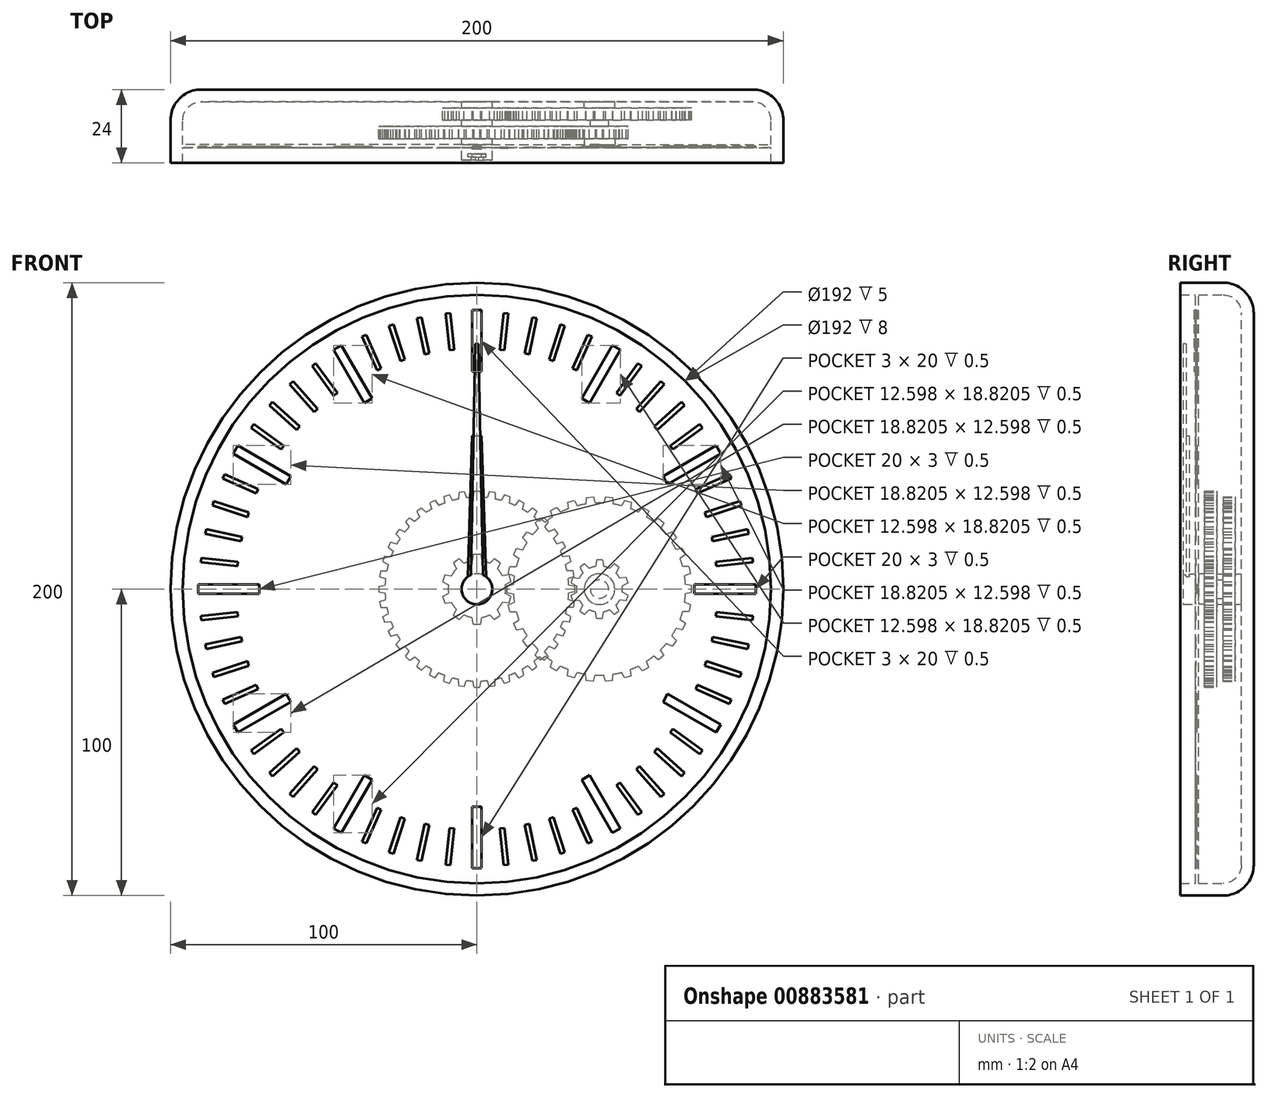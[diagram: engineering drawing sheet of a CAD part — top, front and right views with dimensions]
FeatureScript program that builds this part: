
annotation { "Feature Type Name" : "Feature", "Feature Type Description" : "" }
export const myFeature = defineFeature(function(context is Context, id is Id, definition is map)
    precondition{}
    {
        {
            var Q0;
            Q0=qCreatedBy(makeId("Front.planeOp"),FACE);
            var sketch = newSketch(context, id + "F0", { "sketchPlane" : qUnion([Q0])});
            skCircle(sketch, "E0", {"center": v(0, 0) * mm, "radius": 100 * mm});
            skSolve(sketch);
        }
        {
            var Q0;
            Q0 = qSketchRegion(id + "F0", true);
            extrude(context, id + "F1", {"entities" : qUnion([Q0]), "depth" : 24 * mm, "offsetDistance" : 25 * mm});
        }
        {
            var Q0;
            Q0=makeQuery(id+"F1.opExtrude","CAP_EDGE",EDGE,{"disambiguationData":[OSD([sQuery(id+"F0.wireOp",EDGE,"E0")])],"isStart":true});
            fillet(context, id + "F2", {"entities" : qUnion([Q0]), "radius" : 10 * mm, "tangentPropagation" : true, "allowEdgeOverflow" : false});
        }
        {
            var Q0;
            Q0=makeQuery(id+"F1.opExtrude","CAP_FACE",FACE,{"disambiguationData":[OSD([sQuery(id+"F0.wireOp",EDGE,"E0")])],"isStart":false});
            shell(context, id + "F3", {"entities" : qUnion([Q0]), "thickness" : 4 * mm});
        }
        {
            var Q0;
            {var subQ0=sQuery(id+"F0.wireOp",EDGE,"E0");Q0=makeQuery(id+"F3.opShell","OFFSET_FACE",FACE,{"disambiguationData":[OSD([subQ0]),TDD([makeQuery(id+"F1.opExtrude","CAP_FACE",FACE,{"disambiguationData":[OSD([subQ0])],"isStart":true})])]});}
            var sketch = newSketch(context, id + "F4", { "sketchPlane" : qUnion([Q0])});
            skCircle(sketch, "E1", {"center": v(0, 0) * mm, "radius": 3 * mm});
            skCircle(sketch, "E2", {"center": v(0, 0) * mm, "radius": 5 * mm});
            skCircle(sketch, "E3", {"center": v(40, 0) * mm, "radius": 3 * mm});
            skCircle(sketch, "E4", {"center": v(40, 0) * mm, "radius": 5 * mm});
            skSolve(sketch);
        }
        {
            var Q0;
            Q0 = qSketchRegion(id + "F4", true);
            extrude(context, id + "F5", {"entities" : qUnion([Q0]), "operationType" : NewBodyOperationType.ADD, "depth" : 2 * mm, "offsetDistance" : 25 * mm});
        }
        {
            var Q0;
            {var subQ0=sQuery(id+"F0.wireOp",EDGE,"E0");Q0=makeQuery(id+"F5.boolean.opBoolean","SPLIT",FACE,{"disambiguationData":[TD([makeQuery(id+"F5.opExtrude","SWEPT_FACE",FACE,{"disambiguationData":[OSD([sQuery(id+"F4.wireOp",EDGE,"E1")])]})])],"derivedFrom":makeQuery(id+"F3.opShell","OFFSET_FACE",FACE,{"disambiguationData":[OSD([subQ0]),TDD([makeQuery(id+"F1.opExtrude","CAP_FACE",FACE,{"disambiguationData":[OSD([subQ0])],"isStart":true})])]})});}
            extrude(context, id + "F6", {"entities" : qUnion([Q0]), "depth" : 19 * mm, "offsetDistance" : 25 * mm});
        }
        {
            var Q0;
            {var subQ0=sQuery(id+"F0.wireOp",EDGE,"E0");Q0=makeQuery(id+"F5.boolean.opBoolean","SPLIT",FACE,{"disambiguationData":[TD([makeQuery(id+"F5.opExtrude","SWEPT_FACE",FACE,{"disambiguationData":[OSD([sQuery(id+"F4.wireOp",EDGE,"E3")])]})])],"derivedFrom":makeQuery(id+"F3.opShell","OFFSET_FACE",FACE,{"disambiguationData":[OSD([subQ0]),TDD([makeQuery(id+"F1.opExtrude","CAP_FACE",FACE,{"disambiguationData":[OSD([subQ0])],"isStart":true})])]})});}
            extrude(context, id + "F7", {"entities" : qUnion([Q0]), "depth" : 8 * mm, "offsetDistance" : 25 * mm});
        }
        {
            var Q0;
            Q0=makeQuery(id+"F5.opExtrude","CAP_FACE",FACE,{"disambiguationData":[OSD([sQuery(id+"F4.wireOp",EDGE,"E1"),sQuery(id+"F4.wireOp",EDGE,"E2")])],"isStart":false});
            var sketch = newSketch(context, id + "F8", { "sketchPlane" : qUnion([Q0])});
            skCircle(sketch, "E5", {"center": v(0, 0) * mm, "radius": 9.38 * mm});
            skLineSegment(sketch, "E6", {"start": v(0, 11.38) * mm, "end": v(1.18, 11.38) * mm});
            skLineSegment(sketch, "E7", {"start": v(1.18, 11.38) * mm, "end": v(1.55, 9.25) * mm});
            skLineSegment(sketch, "E8.MirrorCS", {"start": v(0, 11.38) * mm, "end": v(-1.18, 11.38) * mm});
            skLineSegment(sketch, "E9.MirrorCS", {"start": v(-1.18, 11.38) * mm, "end": v(-1.55, 9.25) * mm});
            skLineSegment(sketch, "E10.1.0", {"start": v(-7.64, 8.51) * mm, "end": v(-6.7, 6.57) * mm});
            skLineSegment(sketch, "E10.1.1", {"start": v(-6.69, 9.2) * mm, "end": v(-7.64, 8.51) * mm});
            skLineSegment(sketch, "E10.1.2", {"start": v(-6.69, 9.2) * mm, "end": v(-5.73, 9.9) * mm});
            skLineSegment(sketch, "E10.1.3", {"start": v(-5.73, 9.9) * mm, "end": v(-4.18, 8.4) * mm});
            skLineSegment(sketch, "E10.2.0", {"start": v(-11.18, 2.4) * mm, "end": v(-9.27, 1.38) * mm});
            skLineSegment(sketch, "E10.2.1", {"start": v(-10.82, 3.52) * mm, "end": v(-11.18, 2.4) * mm});
            skLineSegment(sketch, "E10.2.2", {"start": v(-10.82, 3.52) * mm, "end": v(-10.45, 4.64) * mm});
            skLineSegment(sketch, "E10.2.3", {"start": v(-10.45, 4.64) * mm, "end": v(-8.31, 4.33) * mm});
            skLineSegment(sketch, "E11.2.3.0", {"start": v(-10.45, -4.64) * mm, "end": v(-8.31, -4.33) * mm});
            skLineSegment(sketch, "E11.3.3.0", {"start": v(-10.82, -3.52) * mm, "end": v(-10.45, -4.64) * mm});
            skLineSegment(sketch, "E11.6.3.0", {"start": v(-10.82, -3.52) * mm, "end": v(-11.18, -2.4) * mm});
            skLineSegment(sketch, "E11.9.3.0", {"start": v(-11.18, -2.4) * mm, "end": v(-9.27, -1.38) * mm});
            skLineSegment(sketch, "E11.2.4.0", {"start": v(-5.73, -9.9) * mm, "end": v(-4.18, -8.4) * mm});
            skLineSegment(sketch, "E11.3.4.0", {"start": v(-6.69, -9.2) * mm, "end": v(-5.73, -9.9) * mm});
            skLineSegment(sketch, "E11.6.4.0", {"start": v(-6.69, -9.2) * mm, "end": v(-7.64, -8.51) * mm});
            skLineSegment(sketch, "E11.9.4.0", {"start": v(-7.64, -8.51) * mm, "end": v(-6.7, -6.57) * mm});
            skLineSegment(sketch, "E11.2.5.0", {"start": v(1.18, -11.38) * mm, "end": v(1.55, -9.25) * mm});
            skLineSegment(sketch, "E11.3.5.0", {"start": v(0, -11.38) * mm, "end": v(1.18, -11.38) * mm});
            skLineSegment(sketch, "E11.6.5.0", {"start": v(0, -11.38) * mm, "end": v(-1.18, -11.38) * mm});
            skLineSegment(sketch, "E11.9.5.0", {"start": v(-1.18, -11.38) * mm, "end": v(-1.55, -9.25) * mm});
            skLineSegment(sketch, "E11.2.6.0", {"start": v(7.64, -8.51) * mm, "end": v(6.7, -6.57) * mm});
            skLineSegment(sketch, "E11.3.6.0", {"start": v(6.69, -9.2) * mm, "end": v(7.64, -8.51) * mm});
            skLineSegment(sketch, "E11.6.6.0", {"start": v(6.69, -9.2) * mm, "end": v(5.73, -9.9) * mm});
            skLineSegment(sketch, "E11.9.6.0", {"start": v(5.73, -9.9) * mm, "end": v(4.18, -8.4) * mm});
            skLineSegment(sketch, "E11.2.7.0", {"start": v(11.18, -2.4) * mm, "end": v(9.27, -1.38) * mm});
            skLineSegment(sketch, "E11.3.7.0", {"start": v(10.82, -3.52) * mm, "end": v(11.18, -2.4) * mm});
            skLineSegment(sketch, "E11.6.7.0", {"start": v(10.82, -3.52) * mm, "end": v(10.45, -4.64) * mm});
            skLineSegment(sketch, "E11.9.7.0", {"start": v(10.45, -4.64) * mm, "end": v(8.31, -4.33) * mm});
            skLineSegment(sketch, "E11.2.8.0", {"start": v(10.45, 4.64) * mm, "end": v(8.31, 4.33) * mm});
            skLineSegment(sketch, "E11.3.8.0", {"start": v(10.82, 3.52) * mm, "end": v(10.45, 4.64) * mm});
            skLineSegment(sketch, "E11.6.8.0", {"start": v(10.82, 3.52) * mm, "end": v(11.18, 2.4) * mm});
            skLineSegment(sketch, "E11.9.8.0", {"start": v(11.18, 2.4) * mm, "end": v(9.27, 1.38) * mm});
            skLineSegment(sketch, "E11.2.9.0", {"start": v(5.73, 9.9) * mm, "end": v(4.18, 8.4) * mm});
            skLineSegment(sketch, "E11.3.9.0", {"start": v(6.69, 9.2) * mm, "end": v(5.73, 9.9) * mm});
            skLineSegment(sketch, "E11.6.9.0", {"start": v(6.69, 9.2) * mm, "end": v(7.64, 8.51) * mm});
            skLineSegment(sketch, "E11.9.9.0", {"start": v(7.64, 8.51) * mm, "end": v(6.7, 6.57) * mm});
            skSolve(sketch);
        }
        {
            var Q0;
            Q0 = qSketchRegion(id + "F8", true);
            extrude(context, id + "F9", {"entities" : qUnion([Q0]), "operationType" : NewBodyOperationType.ADD, "depth" : 4 * mm, "offsetDistance" : 25 * mm});
        }
        {
            var Q0;
            Q0=makeQuery(id+"F5.opExtrude","CAP_FACE",FACE,{"disambiguationData":[OSD([sQuery(id+"F4.wireOp",EDGE,"E3"),sQuery(id+"F4.wireOp",EDGE,"E4")])],"isStart":false});
            var sketch = newSketch(context, id + "F10", { "sketchPlane" : qUnion([Q0])});
            skCircle(sketch, "E12", {"center": v(40, 0) * mm, "radius": 28.12 * mm});
            skLineSegment(sketch, "E13", {"start": v(9.88, 0) * mm, "end": v(9.88, 1.18) * mm});
            skLineSegment(sketch, "E14", {"start": v(9.88, 1.18) * mm, "end": v(11.92, 1.54) * mm});
            skLineSegment(sketch, "E15.MirrorCS", {"start": v(9.88, 0) * mm, "end": v(9.88, -1.18) * mm});
            skLineSegment(sketch, "E16.MirrorCS", {"start": v(9.88, -1.18) * mm, "end": v(11.92, -1.54) * mm});
            skLineSegment(sketch, "E17.1.0", {"start": v(10.29, -5.11) * mm, "end": v(12.21, -4.33) * mm});
            skLineSegment(sketch, "E17.1.1", {"start": v(10.53, -6.26) * mm, "end": v(10.29, -5.11) * mm});
            skLineSegment(sketch, "E17.1.2", {"start": v(10.53, -6.26) * mm, "end": v(10.78, -7.42) * mm});
            skLineSegment(sketch, "E17.1.3", {"start": v(10.78, -7.42) * mm, "end": v(12.85, -7.34) * mm});
            skLineSegment(sketch, "E17.2.0", {"start": v(12, -11.18) * mm, "end": v(13.72, -10.02) * mm});
            skLineSegment(sketch, "E17.2.1", {"start": v(12.48, -12.25) * mm, "end": v(12, -11.18) * mm});
            skLineSegment(sketch, "E17.2.2", {"start": v(12.48, -12.25) * mm, "end": v(12.96, -13.33) * mm});
            skLineSegment(sketch, "E17.2.3", {"start": v(12.96, -13.33) * mm, "end": v(14.97, -12.83) * mm});
            skLineSegment(sketch, "E18.1.3.0", {"start": v(14.94, -16.75) * mm, "end": v(16.38, -15.26) * mm});
            skLineSegment(sketch, "E18.3.3.0", {"start": v(15.63, -17.7) * mm, "end": v(14.94, -16.75) * mm});
            skLineSegment(sketch, "E18.6.3.0", {"start": v(15.63, -17.7) * mm, "end": v(16.32, -18.66) * mm});
            skLineSegment(sketch, "E18.9.3.0", {"start": v(16.32, -18.66) * mm, "end": v(18.18, -17.75) * mm});
            skLineSegment(sketch, "E18.1.4.0", {"start": v(18.97, -21.6) * mm, "end": v(20.07, -19.84) * mm});
            skLineSegment(sketch, "E18.3.4.0", {"start": v(19.84, -22.39) * mm, "end": v(18.97, -21.6) * mm});
            skLineSegment(sketch, "E18.6.4.0", {"start": v(19.84, -22.39) * mm, "end": v(20.72, -23.18) * mm});
            skLineSegment(sketch, "E18.9.4.0", {"start": v(20.72, -23.18) * mm, "end": v(22.35, -21.9) * mm});
            skLineSegment(sketch, "E18.1.5.0", {"start": v(23.92, -25.5) * mm, "end": v(24.63, -23.55) * mm});
            skLineSegment(sketch, "E18.3.5.0", {"start": v(24.94, -26.09) * mm, "end": v(23.92, -25.5) * mm});
            skLineSegment(sketch, "E18.6.5.0", {"start": v(24.94, -26.09) * mm, "end": v(25.96, -26.68) * mm});
            skLineSegment(sketch, "E18.9.5.0", {"start": v(25.96, -26.68) * mm, "end": v(27.3, -25.09) * mm});
            skLineSegment(sketch, "E18.1.6.0", {"start": v(29.57, -28.29) * mm, "end": v(29.86, -26.23) * mm});
            skLineSegment(sketch, "E18.3.6.0", {"start": v(30.7, -28.65) * mm, "end": v(29.57, -28.29) * mm});
            skLineSegment(sketch, "E18.6.6.0", {"start": v(30.7, -28.65) * mm, "end": v(31.81, -29.01) * mm});
            skLineSegment(sketch, "E18.9.6.0", {"start": v(31.81, -29.01) * mm, "end": v(32.78, -27.18) * mm});
            skLineSegment(sketch, "E18.1.7.0", {"start": v(35.68, -29.84) * mm, "end": v(35.53, -27.77) * mm});
            skLineSegment(sketch, "E18.3.7.0", {"start": v(36.85, -29.96) * mm, "end": v(35.68, -29.84) * mm});
            skLineSegment(sketch, "E18.6.7.0", {"start": v(36.85, -29.96) * mm, "end": v(38.02, -30.08) * mm});
            skLineSegment(sketch, "E18.9.7.0", {"start": v(38.02, -30.08) * mm, "end": v(38.6, -28.09) * mm});
            skLineSegment(sketch, "E18.1.8.0", {"start": v(41.98, -30.08) * mm, "end": v(41.4, -28.09) * mm});
            skLineSegment(sketch, "E18.3.8.0", {"start": v(43.15, -29.96) * mm, "end": v(41.98, -30.08) * mm});
            skLineSegment(sketch, "E18.6.8.0", {"start": v(43.15, -29.96) * mm, "end": v(44.32, -29.84) * mm});
            skLineSegment(sketch, "E18.9.8.0", {"start": v(44.32, -29.84) * mm, "end": v(44.47, -27.77) * mm});
            skLineSegment(sketch, "E18.1.9.0", {"start": v(48.19, -29.01) * mm, "end": v(47.22, -27.18) * mm});
            skLineSegment(sketch, "E18.3.9.0", {"start": v(49.3, -28.65) * mm, "end": v(48.19, -29.01) * mm});
            skLineSegment(sketch, "E18.6.9.0", {"start": v(49.3, -28.65) * mm, "end": v(50.43, -28.29) * mm});
            skLineSegment(sketch, "E18.9.9.0", {"start": v(50.43, -28.29) * mm, "end": v(50.14, -26.23) * mm});
            skLineSegment(sketch, "E18.1.10.0", {"start": v(54.04, -26.68) * mm, "end": v(52.7, -25.09) * mm});
            skLineSegment(sketch, "E18.3.10.0", {"start": v(55.06, -26.09) * mm, "end": v(54.04, -26.68) * mm});
            skLineSegment(sketch, "E18.6.10.0", {"start": v(55.06, -26.09) * mm, "end": v(56.08, -25.5) * mm});
            skLineSegment(sketch, "E18.9.10.0", {"start": v(56.08, -25.5) * mm, "end": v(55.37, -23.55) * mm});
            skLineSegment(sketch, "E18.1.11.0", {"start": v(59.28, -23.18) * mm, "end": v(57.65, -21.9) * mm});
            skLineSegment(sketch, "E18.3.11.0", {"start": v(60.16, -22.39) * mm, "end": v(59.28, -23.18) * mm});
            skLineSegment(sketch, "E18.6.11.0", {"start": v(60.16, -22.39) * mm, "end": v(61.03, -21.6) * mm});
            skLineSegment(sketch, "E18.9.11.0", {"start": v(61.03, -21.6) * mm, "end": v(59.93, -19.84) * mm});
            skLineSegment(sketch, "E18.1.12.0", {"start": v(63.68, -18.66) * mm, "end": v(61.82, -17.75) * mm});
            skLineSegment(sketch, "E18.3.12.0", {"start": v(64.37, -17.7) * mm, "end": v(63.68, -18.66) * mm});
            skLineSegment(sketch, "E18.6.12.0", {"start": v(64.37, -17.7) * mm, "end": v(65.06, -16.75) * mm});
            skLineSegment(sketch, "E18.9.12.0", {"start": v(65.06, -16.75) * mm, "end": v(63.62, -15.26) * mm});
            skLineSegment(sketch, "E18.1.13.0", {"start": v(67.04, -13.33) * mm, "end": v(65.03, -12.83) * mm});
            skLineSegment(sketch, "E18.3.13.0", {"start": v(67.52, -12.25) * mm, "end": v(67.04, -13.33) * mm});
            skLineSegment(sketch, "E18.6.13.0", {"start": v(67.52, -12.25) * mm, "end": v(68, -11.18) * mm});
            skLineSegment(sketch, "E18.9.13.0", {"start": v(68, -11.18) * mm, "end": v(66.28, -10.02) * mm});
            skLineSegment(sketch, "E18.1.14.0", {"start": v(69.22, -7.42) * mm, "end": v(67.15, -7.34) * mm});
            skLineSegment(sketch, "E18.3.14.0", {"start": v(69.47, -6.26) * mm, "end": v(69.22, -7.42) * mm});
            skLineSegment(sketch, "E18.6.14.0", {"start": v(69.47, -6.26) * mm, "end": v(69.71, -5.11) * mm});
            skLineSegment(sketch, "E18.9.14.0", {"start": v(69.71, -5.11) * mm, "end": v(67.79, -4.33) * mm});
            skLineSegment(sketch, "E18.1.15.0", {"start": v(70.12, -1.18) * mm, "end": v(68.08, -1.54) * mm});
            skLineSegment(sketch, "E18.3.15.0", {"start": v(70.12, 0) * mm, "end": v(70.12, -1.18) * mm});
            skLineSegment(sketch, "E18.6.15.0", {"start": v(70.12, 0) * mm, "end": v(70.12, 1.18) * mm});
            skLineSegment(sketch, "E18.9.15.0", {"start": v(70.12, 1.18) * mm, "end": v(68.08, 1.54) * mm});
            skLineSegment(sketch, "E18.1.16.0", {"start": v(69.71, 5.11) * mm, "end": v(67.79, 4.33) * mm});
            skLineSegment(sketch, "E18.3.16.0", {"start": v(69.47, 6.26) * mm, "end": v(69.71, 5.11) * mm});
            skLineSegment(sketch, "E18.6.16.0", {"start": v(69.47, 6.26) * mm, "end": v(69.22, 7.42) * mm});
            skLineSegment(sketch, "E18.9.16.0", {"start": v(69.22, 7.42) * mm, "end": v(67.15, 7.34) * mm});
            skLineSegment(sketch, "E18.1.17.0", {"start": v(68, 11.18) * mm, "end": v(66.28, 10.02) * mm});
            skLineSegment(sketch, "E18.3.17.0", {"start": v(67.52, 12.25) * mm, "end": v(68, 11.18) * mm});
            skLineSegment(sketch, "E18.6.17.0", {"start": v(67.52, 12.25) * mm, "end": v(67.04, 13.33) * mm});
            skLineSegment(sketch, "E18.9.17.0", {"start": v(67.04, 13.33) * mm, "end": v(65.03, 12.83) * mm});
            skLineSegment(sketch, "E18.1.18.0", {"start": v(65.06, 16.75) * mm, "end": v(63.62, 15.26) * mm});
            skLineSegment(sketch, "E18.3.18.0", {"start": v(64.37, 17.7) * mm, "end": v(65.06, 16.75) * mm});
            skLineSegment(sketch, "E18.6.18.0", {"start": v(64.37, 17.7) * mm, "end": v(63.68, 18.66) * mm});
            skLineSegment(sketch, "E18.9.18.0", {"start": v(63.68, 18.66) * mm, "end": v(61.82, 17.75) * mm});
            skLineSegment(sketch, "E18.1.19.0", {"start": v(61.03, 21.6) * mm, "end": v(59.93, 19.84) * mm});
            skLineSegment(sketch, "E18.3.19.0", {"start": v(60.16, 22.39) * mm, "end": v(61.03, 21.6) * mm});
            skLineSegment(sketch, "E18.6.19.0", {"start": v(60.16, 22.39) * mm, "end": v(59.28, 23.18) * mm});
            skLineSegment(sketch, "E18.9.19.0", {"start": v(59.28, 23.18) * mm, "end": v(57.65, 21.9) * mm});
            skLineSegment(sketch, "E18.1.20.0", {"start": v(56.08, 25.5) * mm, "end": v(55.37, 23.55) * mm});
            skLineSegment(sketch, "E18.3.20.0", {"start": v(55.06, 26.09) * mm, "end": v(56.08, 25.5) * mm});
            skLineSegment(sketch, "E18.6.20.0", {"start": v(55.06, 26.09) * mm, "end": v(54.04, 26.68) * mm});
            skLineSegment(sketch, "E18.9.20.0", {"start": v(54.04, 26.68) * mm, "end": v(52.7, 25.09) * mm});
            skLineSegment(sketch, "E18.1.21.0", {"start": v(50.43, 28.29) * mm, "end": v(50.14, 26.23) * mm});
            skLineSegment(sketch, "E18.3.21.0", {"start": v(49.3, 28.65) * mm, "end": v(50.43, 28.29) * mm});
            skLineSegment(sketch, "E18.6.21.0", {"start": v(49.3, 28.65) * mm, "end": v(48.19, 29.01) * mm});
            skLineSegment(sketch, "E18.9.21.0", {"start": v(48.19, 29.01) * mm, "end": v(47.22, 27.18) * mm});
            skLineSegment(sketch, "E18.1.22.0", {"start": v(44.32, 29.84) * mm, "end": v(44.47, 27.77) * mm});
            skLineSegment(sketch, "E18.3.22.0", {"start": v(43.15, 29.96) * mm, "end": v(44.32, 29.84) * mm});
            skLineSegment(sketch, "E18.6.22.0", {"start": v(43.15, 29.96) * mm, "end": v(41.98, 30.08) * mm});
            skLineSegment(sketch, "E18.9.22.0", {"start": v(41.98, 30.08) * mm, "end": v(41.4, 28.09) * mm});
            skLineSegment(sketch, "E18.1.23.0", {"start": v(38.02, 30.08) * mm, "end": v(38.6, 28.09) * mm});
            skLineSegment(sketch, "E18.3.23.0", {"start": v(36.85, 29.96) * mm, "end": v(38.02, 30.08) * mm});
            skLineSegment(sketch, "E18.6.23.0", {"start": v(36.85, 29.96) * mm, "end": v(35.68, 29.84) * mm});
            skLineSegment(sketch, "E18.9.23.0", {"start": v(35.68, 29.84) * mm, "end": v(35.53, 27.77) * mm});
            skLineSegment(sketch, "E18.1.24.0", {"start": v(31.81, 29.01) * mm, "end": v(32.78, 27.18) * mm});
            skLineSegment(sketch, "E18.3.24.0", {"start": v(30.7, 28.65) * mm, "end": v(31.81, 29.01) * mm});
            skLineSegment(sketch, "E18.6.24.0", {"start": v(30.7, 28.65) * mm, "end": v(29.57, 28.29) * mm});
            skLineSegment(sketch, "E18.9.24.0", {"start": v(29.57, 28.29) * mm, "end": v(29.86, 26.23) * mm});
            skLineSegment(sketch, "E18.1.25.0", {"start": v(25.96, 26.68) * mm, "end": v(27.3, 25.09) * mm});
            skLineSegment(sketch, "E18.3.25.0", {"start": v(24.94, 26.09) * mm, "end": v(25.96, 26.68) * mm});
            skLineSegment(sketch, "E18.6.25.0", {"start": v(24.94, 26.09) * mm, "end": v(23.92, 25.5) * mm});
            skLineSegment(sketch, "E18.9.25.0", {"start": v(23.92, 25.5) * mm, "end": v(24.63, 23.55) * mm});
            skLineSegment(sketch, "E18.1.26.0", {"start": v(20.72, 23.18) * mm, "end": v(22.35, 21.9) * mm});
            skLineSegment(sketch, "E18.3.26.0", {"start": v(19.84, 22.39) * mm, "end": v(20.72, 23.18) * mm});
            skLineSegment(sketch, "E18.6.26.0", {"start": v(19.84, 22.39) * mm, "end": v(18.97, 21.6) * mm});
            skLineSegment(sketch, "E18.9.26.0", {"start": v(18.97, 21.6) * mm, "end": v(20.07, 19.84) * mm});
            skLineSegment(sketch, "E18.1.27.0", {"start": v(16.32, 18.66) * mm, "end": v(18.18, 17.75) * mm});
            skLineSegment(sketch, "E18.3.27.0", {"start": v(15.63, 17.7) * mm, "end": v(16.32, 18.66) * mm});
            skLineSegment(sketch, "E18.6.27.0", {"start": v(15.63, 17.7) * mm, "end": v(14.94, 16.75) * mm});
            skLineSegment(sketch, "E18.9.27.0", {"start": v(14.94, 16.75) * mm, "end": v(16.38, 15.26) * mm});
            skLineSegment(sketch, "E18.1.28.0", {"start": v(12.96, 13.33) * mm, "end": v(14.97, 12.83) * mm});
            skLineSegment(sketch, "E18.3.28.0", {"start": v(12.48, 12.25) * mm, "end": v(12.96, 13.33) * mm});
            skLineSegment(sketch, "E18.6.28.0", {"start": v(12.48, 12.25) * mm, "end": v(12, 11.18) * mm});
            skLineSegment(sketch, "E18.9.28.0", {"start": v(12, 11.18) * mm, "end": v(13.72, 10.02) * mm});
            skLineSegment(sketch, "E18.1.29.0", {"start": v(10.78, 7.42) * mm, "end": v(12.85, 7.34) * mm});
            skLineSegment(sketch, "E18.3.29.0", {"start": v(10.53, 6.26) * mm, "end": v(10.78, 7.42) * mm});
            skLineSegment(sketch, "E18.6.29.0", {"start": v(10.53, 6.26) * mm, "end": v(10.29, 5.11) * mm});
            skLineSegment(sketch, "E18.9.29.0", {"start": v(10.29, 5.11) * mm, "end": v(12.21, 4.33) * mm});
            skSolve(sketch);
        }
        {
            var Q0;
            Q0 = qSketchRegion(id + "F10", true);
            extrude(context, id + "F11", {"entities" : qUnion([Q0]), "operationType" : NewBodyOperationType.ADD, "depth" : 4 * mm, "offsetDistance" : 25 * mm});
        }
        {
            var Q0;
            Q0=makeQuery(id+"F9.opExtrude","CAP_FACE",FACE,{"disambiguationData":[OSD([sQuery(id+"F8.wireOp",EDGE,"E5"),sQuery(id+"F8.wireOp",EDGE,"E6"),sQuery(id+"F8.wireOp",EDGE,"E7"),sQuery(id+"F8.wireOp",EDGE,"E8.MirrorCS"),sQuery(id+"F8.wireOp",EDGE,"E9.MirrorCS"),sQuery(id+"F8.wireOp",EDGE,"E10.1.0"),sQuery(id+"F8.wireOp",EDGE,"E10.1.1"),sQuery(id+"F8.wireOp",EDGE,"E10.1.2"),sQuery(id+"F8.wireOp",EDGE,"E10.1.3"),sQuery(id+"F8.wireOp",EDGE,"E10.2.0"),sQuery(id+"F8.wireOp",EDGE,"E10.2.1"),sQuery(id+"F8.wireOp",EDGE,"E10.2.2"),sQuery(id+"F8.wireOp",EDGE,"E10.2.3"),sQuery(id+"F8.wireOp",EDGE,"E11.2.3.0"),sQuery(id+"F8.wireOp",EDGE,"E11.3.3.0"),sQuery(id+"F8.wireOp",EDGE,"E11.6.3.0"),sQuery(id+"F8.wireOp",EDGE,"E11.9.3.0"),sQuery(id+"F8.wireOp",EDGE,"E11.2.4.0"),sQuery(id+"F8.wireOp",EDGE,"E11.3.4.0"),sQuery(id+"F8.wireOp",EDGE,"E11.6.4.0"),sQuery(id+"F8.wireOp",EDGE,"E11.9.4.0"),sQuery(id+"F8.wireOp",EDGE,"E11.2.5.0"),sQuery(id+"F8.wireOp",EDGE,"E11.3.5.0"),sQuery(id+"F8.wireOp",EDGE,"E11.6.5.0"),sQuery(id+"F8.wireOp",EDGE,"E11.9.5.0"),sQuery(id+"F8.wireOp",EDGE,"E11.2.6.0"),sQuery(id+"F8.wireOp",EDGE,"E11.3.6.0"),sQuery(id+"F8.wireOp",EDGE,"E11.6.6.0"),sQuery(id+"F8.wireOp",EDGE,"E11.9.6.0"),sQuery(id+"F8.wireOp",EDGE,"E11.2.7.0"),sQuery(id+"F8.wireOp",EDGE,"E11.3.7.0"),sQuery(id+"F8.wireOp",EDGE,"E11.6.7.0"),sQuery(id+"F8.wireOp",EDGE,"E11.9.7.0"),sQuery(id+"F8.wireOp",EDGE,"E11.2.8.0"),sQuery(id+"F8.wireOp",EDGE,"E11.3.8.0"),sQuery(id+"F8.wireOp",EDGE,"E11.6.8.0"),sQuery(id+"F8.wireOp",EDGE,"E11.9.8.0"),sQuery(id+"F8.wireOp",EDGE,"E11.2.9.0"),sQuery(id+"F8.wireOp",EDGE,"E11.3.9.0"),sQuery(id+"F8.wireOp",EDGE,"E11.6.9.0"),sQuery(id+"F8.wireOp",EDGE,"E11.9.9.0")])],"isStart":false});
            var sketch = newSketch(context, id + "F12", { "sketchPlane" : qUnion([Q0])});
            skCircle(sketch, "E19.0.0", {"center": v(0, 0) * mm, "radius": 3 * mm});
            skCircle(sketch, "E20.0", {"center": v(0, 0) * mm, "radius": 5 * mm});
            skSolve(sketch);
        }
        {
            var Q0;
            Q0 = qSketchRegion(id + "F12", true);
            extrude(context, id + "F13", {"entities" : qUnion([Q0]), "depth" : 2 * mm, "offsetDistance" : 25 * mm});
        }
        {
            var Q0;
            Q0=makeQuery(id+"F13.opExtrude","CAP_FACE",FACE,{"disambiguationData":[OSD([sQuery(id+"F12.wireOp",EDGE,"E19.0.0"),sQuery(id+"F12.wireOp",EDGE,"E20.0")])],"isStart":false});
            var sketch = newSketch(context, id + "F14", { "sketchPlane" : qUnion([Q0])});
            skCircle(sketch, "E21.0", {"center": v(0, 0) * mm, "radius": 3 * mm});
            skCircle(sketch, "E22", {"center": v(0, 0) * mm, "radius": 30 * mm});
            skLineSegment(sketch, "E23", {"start": v(0, 32) * mm, "end": v(0.94, 32) * mm});
            skLineSegment(sketch, "E24", {"start": v(0.94, 32) * mm, "end": v(1.3, 29.97) * mm});
            skLineSegment(sketch, "E25.MirrorCS", {"start": v(0, 32) * mm, "end": v(-0.94, 32) * mm});
            skLineSegment(sketch, "E26.MirrorCS", {"start": v(-0.94, 32) * mm, "end": v(-1.3, 29.97) * mm});
            skLineSegment(sketch, "E27.1.0", {"start": v(-5, 31.6) * mm, "end": v(-4.08, 31.75) * mm});
            skLineSegment(sketch, "E27.1.1", {"start": v(-5, 31.6) * mm, "end": v(-5.94, 31.46) * mm});
            skLineSegment(sketch, "E27.1.2", {"start": v(-5.94, 31.46) * mm, "end": v(-5.97, 29.4) * mm});
            skLineSegment(sketch, "E27.1.3", {"start": v(-4.08, 31.75) * mm, "end": v(-3.4, 29.8) * mm});
            skLineSegment(sketch, "E27.2.0", {"start": v(-9.89, 30.43) * mm, "end": v(-9, 30.73) * mm});
            skLineSegment(sketch, "E27.2.1", {"start": v(-9.89, 30.43) * mm, "end": v(-10.78, 30.14) * mm});
            skLineSegment(sketch, "E27.2.2", {"start": v(-10.78, 30.14) * mm, "end": v(-10.5, 28.1) * mm});
            skLineSegment(sketch, "E27.2.3", {"start": v(-9, 30.73) * mm, "end": v(-8.03, 28.9) * mm});
            skLineSegment(sketch, "E28.1.3.0", {"start": v(-14.53, 28.51) * mm, "end": v(-13.69, 28.94) * mm});
            skLineSegment(sketch, "E28.3.3.0", {"start": v(-14.53, 28.51) * mm, "end": v(-15.37, 28.08) * mm});
            skLineSegment(sketch, "E28.6.3.0", {"start": v(-15.37, 28.08) * mm, "end": v(-14.77, 26.11) * mm});
            skLineSegment(sketch, "E28.9.3.0", {"start": v(-13.69, 28.94) * mm, "end": v(-12.45, 27.3) * mm});
            skLineSegment(sketch, "E28.1.4.0", {"start": v(-18.8, 25.89) * mm, "end": v(-18.05, 26.44) * mm});
            skLineSegment(sketch, "E28.3.4.0", {"start": v(-18.8, 25.89) * mm, "end": v(-19.57, 25.33) * mm});
            skLineSegment(sketch, "E28.6.4.0", {"start": v(-19.57, 25.33) * mm, "end": v(-18.67, 23.48) * mm});
            skLineSegment(sketch, "E28.9.4.0", {"start": v(-18.05, 26.44) * mm, "end": v(-16.57, 25.01) * mm});
            skLineSegment(sketch, "E28.1.5.0", {"start": v(-22.63, 22.63) * mm, "end": v(-21.96, 23.3) * mm});
            skLineSegment(sketch, "E28.3.5.0", {"start": v(-22.63, 22.63) * mm, "end": v(-23.3, 21.96) * mm});
            skLineSegment(sketch, "E28.6.5.0", {"start": v(-23.3, 21.96) * mm, "end": v(-22.11, 20.27) * mm});
            skLineSegment(sketch, "E28.9.5.0", {"start": v(-21.96, 23.3) * mm, "end": v(-20.27, 22.11) * mm});
            skLineSegment(sketch, "E28.1.6.0", {"start": v(-25.89, 18.8) * mm, "end": v(-25.33, 19.57) * mm});
            skLineSegment(sketch, "E28.3.6.0", {"start": v(-25.89, 18.8) * mm, "end": v(-26.44, 18.05) * mm});
            skLineSegment(sketch, "E28.6.6.0", {"start": v(-26.44, 18.05) * mm, "end": v(-25.01, 16.57) * mm});
            skLineSegment(sketch, "E28.9.6.0", {"start": v(-25.33, 19.57) * mm, "end": v(-23.48, 18.67) * mm});
            skLineSegment(sketch, "E28.1.7.0", {"start": v(-28.51, 14.53) * mm, "end": v(-28.08, 15.37) * mm});
            skLineSegment(sketch, "E28.3.7.0", {"start": v(-28.51, 14.53) * mm, "end": v(-28.94, 13.69) * mm});
            skLineSegment(sketch, "E28.6.7.0", {"start": v(-28.94, 13.69) * mm, "end": v(-27.3, 12.45) * mm});
            skLineSegment(sketch, "E28.9.7.0", {"start": v(-28.08, 15.37) * mm, "end": v(-26.11, 14.77) * mm});
            skLineSegment(sketch, "E28.1.8.0", {"start": v(-30.43, 9.89) * mm, "end": v(-30.14, 10.78) * mm});
            skLineSegment(sketch, "E28.3.8.0", {"start": v(-30.43, 9.89) * mm, "end": v(-30.73, 9) * mm});
            skLineSegment(sketch, "E28.6.8.0", {"start": v(-30.73, 9) * mm, "end": v(-28.9, 8.03) * mm});
            skLineSegment(sketch, "E28.9.8.0", {"start": v(-30.14, 10.78) * mm, "end": v(-28.1, 10.5) * mm});
            skLineSegment(sketch, "E28.1.9.0", {"start": v(-31.6, 5) * mm, "end": v(-31.46, 5.94) * mm});
            skLineSegment(sketch, "E28.3.9.0", {"start": v(-31.6, 5) * mm, "end": v(-31.75, 4.08) * mm});
            skLineSegment(sketch, "E28.6.9.0", {"start": v(-31.75, 4.08) * mm, "end": v(-29.8, 3.4) * mm});
            skLineSegment(sketch, "E28.9.9.0", {"start": v(-31.46, 5.94) * mm, "end": v(-29.4, 5.97) * mm});
            skLineSegment(sketch, "E28.1.10.0", {"start": v(-32, 0) * mm, "end": v(-32, 0.94) * mm});
            skLineSegment(sketch, "E28.3.10.0", {"start": v(-32, 0) * mm, "end": v(-32, -0.94) * mm});
            skLineSegment(sketch, "E28.6.10.0", {"start": v(-32, -0.94) * mm, "end": v(-29.97, -1.3) * mm});
            skLineSegment(sketch, "E28.9.10.0", {"start": v(-32, 0.94) * mm, "end": v(-29.97, 1.3) * mm});
            skLineSegment(sketch, "E28.1.11.0", {"start": v(-31.6, -5) * mm, "end": v(-31.75, -4.08) * mm});
            skLineSegment(sketch, "E28.3.11.0", {"start": v(-31.6, -5) * mm, "end": v(-31.46, -5.94) * mm});
            skLineSegment(sketch, "E28.6.11.0", {"start": v(-31.46, -5.94) * mm, "end": v(-29.4, -5.97) * mm});
            skLineSegment(sketch, "E28.9.11.0", {"start": v(-31.75, -4.08) * mm, "end": v(-29.8, -3.4) * mm});
            skLineSegment(sketch, "E28.1.12.0", {"start": v(-30.43, -9.89) * mm, "end": v(-30.73, -9) * mm});
            skLineSegment(sketch, "E28.3.12.0", {"start": v(-30.43, -9.89) * mm, "end": v(-30.14, -10.78) * mm});
            skLineSegment(sketch, "E28.6.12.0", {"start": v(-30.14, -10.78) * mm, "end": v(-28.1, -10.5) * mm});
            skLineSegment(sketch, "E28.9.12.0", {"start": v(-30.73, -9) * mm, "end": v(-28.9, -8.03) * mm});
            skLineSegment(sketch, "E28.1.13.0", {"start": v(-28.51, -14.53) * mm, "end": v(-28.94, -13.69) * mm});
            skLineSegment(sketch, "E28.3.13.0", {"start": v(-28.51, -14.53) * mm, "end": v(-28.08, -15.37) * mm});
            skLineSegment(sketch, "E28.6.13.0", {"start": v(-28.08, -15.37) * mm, "end": v(-26.11, -14.77) * mm});
            skLineSegment(sketch, "E28.9.13.0", {"start": v(-28.94, -13.69) * mm, "end": v(-27.3, -12.45) * mm});
            skLineSegment(sketch, "E28.1.14.0", {"start": v(-25.89, -18.8) * mm, "end": v(-26.44, -18.05) * mm});
            skLineSegment(sketch, "E28.3.14.0", {"start": v(-25.89, -18.8) * mm, "end": v(-25.33, -19.57) * mm});
            skLineSegment(sketch, "E28.6.14.0", {"start": v(-25.33, -19.57) * mm, "end": v(-23.48, -18.67) * mm});
            skLineSegment(sketch, "E28.9.14.0", {"start": v(-26.44, -18.05) * mm, "end": v(-25.01, -16.57) * mm});
            skLineSegment(sketch, "E28.1.15.0", {"start": v(-22.63, -22.63) * mm, "end": v(-23.3, -21.96) * mm});
            skLineSegment(sketch, "E28.3.15.0", {"start": v(-22.63, -22.63) * mm, "end": v(-21.96, -23.3) * mm});
            skLineSegment(sketch, "E28.6.15.0", {"start": v(-21.96, -23.3) * mm, "end": v(-20.27, -22.11) * mm});
            skLineSegment(sketch, "E28.9.15.0", {"start": v(-23.3, -21.96) * mm, "end": v(-22.11, -20.27) * mm});
            skLineSegment(sketch, "E28.1.16.0", {"start": v(-18.8, -25.89) * mm, "end": v(-19.57, -25.33) * mm});
            skLineSegment(sketch, "E28.3.16.0", {"start": v(-18.8, -25.89) * mm, "end": v(-18.05, -26.44) * mm});
            skLineSegment(sketch, "E28.6.16.0", {"start": v(-18.05, -26.44) * mm, "end": v(-16.57, -25.01) * mm});
            skLineSegment(sketch, "E28.9.16.0", {"start": v(-19.57, -25.33) * mm, "end": v(-18.67, -23.48) * mm});
            skLineSegment(sketch, "E28.1.17.0", {"start": v(-14.53, -28.51) * mm, "end": v(-15.37, -28.08) * mm});
            skLineSegment(sketch, "E28.3.17.0", {"start": v(-14.53, -28.51) * mm, "end": v(-13.69, -28.94) * mm});
            skLineSegment(sketch, "E28.6.17.0", {"start": v(-13.69, -28.94) * mm, "end": v(-12.45, -27.3) * mm});
            skLineSegment(sketch, "E28.9.17.0", {"start": v(-15.37, -28.08) * mm, "end": v(-14.77, -26.11) * mm});
            skLineSegment(sketch, "E28.1.18.0", {"start": v(-9.89, -30.43) * mm, "end": v(-10.78, -30.14) * mm});
            skLineSegment(sketch, "E28.3.18.0", {"start": v(-9.89, -30.43) * mm, "end": v(-9, -30.73) * mm});
            skLineSegment(sketch, "E28.6.18.0", {"start": v(-9, -30.73) * mm, "end": v(-8.03, -28.9) * mm});
            skLineSegment(sketch, "E28.9.18.0", {"start": v(-10.78, -30.14) * mm, "end": v(-10.5, -28.1) * mm});
            skLineSegment(sketch, "E28.1.19.0", {"start": v(-5, -31.6) * mm, "end": v(-5.94, -31.46) * mm});
            skLineSegment(sketch, "E28.3.19.0", {"start": v(-5, -31.6) * mm, "end": v(-4.08, -31.75) * mm});
            skLineSegment(sketch, "E28.6.19.0", {"start": v(-4.08, -31.75) * mm, "end": v(-3.4, -29.8) * mm});
            skLineSegment(sketch, "E28.9.19.0", {"start": v(-5.94, -31.46) * mm, "end": v(-5.97, -29.4) * mm});
            skLineSegment(sketch, "E28.1.20.0", {"start": v(0, -32) * mm, "end": v(-0.94, -32) * mm});
            skLineSegment(sketch, "E28.3.20.0", {"start": v(0, -32) * mm, "end": v(0.94, -32) * mm});
            skLineSegment(sketch, "E28.6.20.0", {"start": v(0.94, -32) * mm, "end": v(1.3, -29.97) * mm});
            skLineSegment(sketch, "E28.9.20.0", {"start": v(-0.94, -32) * mm, "end": v(-1.3, -29.97) * mm});
            skLineSegment(sketch, "E28.1.21.0", {"start": v(5, -31.6) * mm, "end": v(4.08, -31.75) * mm});
            skLineSegment(sketch, "E28.3.21.0", {"start": v(5, -31.6) * mm, "end": v(5.94, -31.46) * mm});
            skLineSegment(sketch, "E28.6.21.0", {"start": v(5.94, -31.46) * mm, "end": v(5.97, -29.4) * mm});
            skLineSegment(sketch, "E28.9.21.0", {"start": v(4.08, -31.75) * mm, "end": v(3.4, -29.8) * mm});
            skLineSegment(sketch, "E28.1.22.0", {"start": v(9.89, -30.43) * mm, "end": v(9, -30.73) * mm});
            skLineSegment(sketch, "E28.3.22.0", {"start": v(9.89, -30.43) * mm, "end": v(10.78, -30.14) * mm});
            skLineSegment(sketch, "E28.6.22.0", {"start": v(10.78, -30.14) * mm, "end": v(10.5, -28.1) * mm});
            skLineSegment(sketch, "E28.9.22.0", {"start": v(9, -30.73) * mm, "end": v(8.03, -28.9) * mm});
            skLineSegment(sketch, "E28.1.23.0", {"start": v(14.53, -28.51) * mm, "end": v(13.69, -28.94) * mm});
            skLineSegment(sketch, "E28.3.23.0", {"start": v(14.53, -28.51) * mm, "end": v(15.37, -28.08) * mm});
            skLineSegment(sketch, "E28.6.23.0", {"start": v(15.37, -28.08) * mm, "end": v(14.77, -26.11) * mm});
            skLineSegment(sketch, "E28.9.23.0", {"start": v(13.69, -28.94) * mm, "end": v(12.45, -27.3) * mm});
            skLineSegment(sketch, "E28.1.24.0", {"start": v(18.8, -25.89) * mm, "end": v(18.05, -26.44) * mm});
            skLineSegment(sketch, "E28.3.24.0", {"start": v(18.8, -25.89) * mm, "end": v(19.57, -25.33) * mm});
            skLineSegment(sketch, "E28.6.24.0", {"start": v(19.57, -25.33) * mm, "end": v(18.67, -23.48) * mm});
            skLineSegment(sketch, "E28.9.24.0", {"start": v(18.05, -26.44) * mm, "end": v(16.57, -25.01) * mm});
            skLineSegment(sketch, "E28.1.25.0", {"start": v(22.63, -22.63) * mm, "end": v(21.96, -23.3) * mm});
            skLineSegment(sketch, "E28.3.25.0", {"start": v(22.63, -22.63) * mm, "end": v(23.3, -21.96) * mm});
            skLineSegment(sketch, "E28.6.25.0", {"start": v(23.3, -21.96) * mm, "end": v(22.11, -20.27) * mm});
            skLineSegment(sketch, "E28.9.25.0", {"start": v(21.96, -23.3) * mm, "end": v(20.27, -22.11) * mm});
            skLineSegment(sketch, "E28.1.26.0", {"start": v(25.89, -18.8) * mm, "end": v(25.33, -19.57) * mm});
            skLineSegment(sketch, "E28.3.26.0", {"start": v(25.89, -18.8) * mm, "end": v(26.44, -18.05) * mm});
            skLineSegment(sketch, "E28.6.26.0", {"start": v(26.44, -18.05) * mm, "end": v(25.01, -16.57) * mm});
            skLineSegment(sketch, "E28.9.26.0", {"start": v(25.33, -19.57) * mm, "end": v(23.48, -18.67) * mm});
            skLineSegment(sketch, "E28.1.27.0", {"start": v(28.51, -14.53) * mm, "end": v(28.08, -15.37) * mm});
            skLineSegment(sketch, "E28.3.27.0", {"start": v(28.51, -14.53) * mm, "end": v(28.94, -13.69) * mm});
            skLineSegment(sketch, "E28.6.27.0", {"start": v(28.94, -13.69) * mm, "end": v(27.3, -12.45) * mm});
            skLineSegment(sketch, "E28.9.27.0", {"start": v(28.08, -15.37) * mm, "end": v(26.11, -14.77) * mm});
            skLineSegment(sketch, "E28.1.28.0", {"start": v(30.43, -9.89) * mm, "end": v(30.14, -10.78) * mm});
            skLineSegment(sketch, "E28.3.28.0", {"start": v(30.43, -9.89) * mm, "end": v(30.73, -9) * mm});
            skLineSegment(sketch, "E28.6.28.0", {"start": v(30.73, -9) * mm, "end": v(28.9, -8.03) * mm});
            skLineSegment(sketch, "E28.9.28.0", {"start": v(30.14, -10.78) * mm, "end": v(28.1, -10.5) * mm});
            skLineSegment(sketch, "E28.1.29.0", {"start": v(31.6, -5) * mm, "end": v(31.46, -5.94) * mm});
            skLineSegment(sketch, "E28.3.29.0", {"start": v(31.6, -5) * mm, "end": v(31.75, -4.08) * mm});
            skLineSegment(sketch, "E28.6.29.0", {"start": v(31.75, -4.08) * mm, "end": v(29.8, -3.4) * mm});
            skLineSegment(sketch, "E28.9.29.0", {"start": v(31.46, -5.94) * mm, "end": v(29.4, -5.97) * mm});
            skLineSegment(sketch, "E28.1.30.0", {"start": v(32, 0) * mm, "end": v(32, -0.94) * mm});
            skLineSegment(sketch, "E28.3.30.0", {"start": v(32, 0) * mm, "end": v(32, 0.94) * mm});
            skLineSegment(sketch, "E28.6.30.0", {"start": v(32, 0.94) * mm, "end": v(29.97, 1.3) * mm});
            skLineSegment(sketch, "E28.9.30.0", {"start": v(32, -0.94) * mm, "end": v(29.97, -1.3) * mm});
            skLineSegment(sketch, "E28.1.31.0", {"start": v(31.6, 5) * mm, "end": v(31.75, 4.08) * mm});
            skLineSegment(sketch, "E28.3.31.0", {"start": v(31.6, 5) * mm, "end": v(31.46, 5.94) * mm});
            skLineSegment(sketch, "E28.6.31.0", {"start": v(31.46, 5.94) * mm, "end": v(29.4, 5.97) * mm});
            skLineSegment(sketch, "E28.9.31.0", {"start": v(31.75, 4.08) * mm, "end": v(29.8, 3.4) * mm});
            skLineSegment(sketch, "E28.1.32.0", {"start": v(30.43, 9.89) * mm, "end": v(30.73, 9) * mm});
            skLineSegment(sketch, "E28.3.32.0", {"start": v(30.43, 9.89) * mm, "end": v(30.14, 10.78) * mm});
            skLineSegment(sketch, "E28.6.32.0", {"start": v(30.14, 10.78) * mm, "end": v(28.1, 10.5) * mm});
            skLineSegment(sketch, "E28.9.32.0", {"start": v(30.73, 9) * mm, "end": v(28.9, 8.03) * mm});
            skLineSegment(sketch, "E28.1.33.0", {"start": v(28.51, 14.53) * mm, "end": v(28.94, 13.69) * mm});
            skLineSegment(sketch, "E28.3.33.0", {"start": v(28.51, 14.53) * mm, "end": v(28.08, 15.37) * mm});
            skLineSegment(sketch, "E28.6.33.0", {"start": v(28.08, 15.37) * mm, "end": v(26.11, 14.77) * mm});
            skLineSegment(sketch, "E28.9.33.0", {"start": v(28.94, 13.69) * mm, "end": v(27.3, 12.45) * mm});
            skLineSegment(sketch, "E28.1.34.0", {"start": v(25.89, 18.8) * mm, "end": v(26.44, 18.05) * mm});
            skLineSegment(sketch, "E28.3.34.0", {"start": v(25.89, 18.8) * mm, "end": v(25.33, 19.57) * mm});
            skLineSegment(sketch, "E28.6.34.0", {"start": v(25.33, 19.57) * mm, "end": v(23.48, 18.67) * mm});
            skLineSegment(sketch, "E28.9.34.0", {"start": v(26.44, 18.05) * mm, "end": v(25.01, 16.57) * mm});
            skLineSegment(sketch, "E28.1.35.0", {"start": v(22.63, 22.63) * mm, "end": v(23.3, 21.96) * mm});
            skLineSegment(sketch, "E28.3.35.0", {"start": v(22.63, 22.63) * mm, "end": v(21.96, 23.3) * mm});
            skLineSegment(sketch, "E28.6.35.0", {"start": v(21.96, 23.3) * mm, "end": v(20.27, 22.11) * mm});
            skLineSegment(sketch, "E28.9.35.0", {"start": v(23.3, 21.96) * mm, "end": v(22.11, 20.27) * mm});
            skLineSegment(sketch, "E28.1.36.0", {"start": v(18.8, 25.89) * mm, "end": v(19.57, 25.33) * mm});
            skLineSegment(sketch, "E28.3.36.0", {"start": v(18.8, 25.89) * mm, "end": v(18.05, 26.44) * mm});
            skLineSegment(sketch, "E28.6.36.0", {"start": v(18.05, 26.44) * mm, "end": v(16.57, 25.01) * mm});
            skLineSegment(sketch, "E28.9.36.0", {"start": v(19.57, 25.33) * mm, "end": v(18.67, 23.48) * mm});
            skLineSegment(sketch, "E28.1.37.0", {"start": v(14.53, 28.51) * mm, "end": v(15.37, 28.08) * mm});
            skLineSegment(sketch, "E28.3.37.0", {"start": v(14.53, 28.51) * mm, "end": v(13.69, 28.94) * mm});
            skLineSegment(sketch, "E28.6.37.0", {"start": v(13.69, 28.94) * mm, "end": v(12.45, 27.3) * mm});
            skLineSegment(sketch, "E28.9.37.0", {"start": v(15.37, 28.08) * mm, "end": v(14.77, 26.11) * mm});
            skLineSegment(sketch, "E28.1.38.0", {"start": v(9.89, 30.43) * mm, "end": v(10.78, 30.14) * mm});
            skLineSegment(sketch, "E28.3.38.0", {"start": v(9.89, 30.43) * mm, "end": v(9, 30.73) * mm});
            skLineSegment(sketch, "E28.6.38.0", {"start": v(9, 30.73) * mm, "end": v(8.03, 28.9) * mm});
            skLineSegment(sketch, "E28.9.38.0", {"start": v(10.78, 30.14) * mm, "end": v(10.5, 28.1) * mm});
            skLineSegment(sketch, "E28.1.39.0", {"start": v(5, 31.6) * mm, "end": v(5.94, 31.46) * mm});
            skLineSegment(sketch, "E28.3.39.0", {"start": v(5, 31.6) * mm, "end": v(4.08, 31.75) * mm});
            skLineSegment(sketch, "E28.6.39.0", {"start": v(4.08, 31.75) * mm, "end": v(3.4, 29.8) * mm});
            skLineSegment(sketch, "E28.9.39.0", {"start": v(5.94, 31.46) * mm, "end": v(5.97, 29.4) * mm});
            skSolve(sketch);
        }
        {
            var Q0;
            Q0 = qSketchRegion(id + "F14", true);
            extrude(context, id + "F15", {"entities" : qUnion([Q0]), "operationType" : NewBodyOperationType.ADD, "depth" : 4 * mm, "offsetDistance" : 25 * mm});
        }
        {
            var Q0;
            Q0=makeQuery(id+"F7.opExtrude","CAP_FACE",FACE,{"disambiguationData":[OSD([sQuery(id+"F0.wireOp",EDGE,"E0")])],"isStart":false});
            var sketch = newSketch(context, id + "F16", { "sketchPlane" : qUnion([Q0])});
            skCircle(sketch, "E29", {"center": v(40, 0) * mm, "radius": 7.5 * mm});
            skLineSegment(sketch, "E30", {"start": v(40, 0) * mm, "end": v(40, 7.5) * mm, "construction": true});
            skLineSegment(sketch, "E31", {"start": v(40.94, 9.5) * mm, "end": v(39.06, 9.5) * mm});
            skLineSegment(sketch, "E32", {"start": v(39.06, 9.5) * mm, "end": v(38.68, 7.38) * mm});
            skLineSegment(sketch, "E33.MirrorCS", {"start": v(40.94, 9.5) * mm, "end": v(41.32, 7.38) * mm});
            skLineSegment(sketch, "E34.1.0", {"start": v(35.18, 8.24) * mm, "end": v(33.65, 7.13) * mm});
            skLineSegment(sketch, "E34.1.1", {"start": v(33.65, 7.13) * mm, "end": v(34.6, 5.2) * mm});
            skLineSegment(sketch, "E34.1.2", {"start": v(35.18, 8.24) * mm, "end": v(36.72, 6.75) * mm});
            skLineSegment(sketch, "E34.2.0", {"start": v(31.26, 3.83) * mm, "end": v(30.67, 2.04) * mm});
            skLineSegment(sketch, "E34.2.1", {"start": v(30.67, 2.04) * mm, "end": v(32.57, 1.03) * mm});
            skLineSegment(sketch, "E34.2.2", {"start": v(31.26, 3.83) * mm, "end": v(33.38, 3.53) * mm});
            skLineSegment(sketch, "E35.2.3.0", {"start": v(30.67, -2.04) * mm, "end": v(31.26, -3.83) * mm});
            skLineSegment(sketch, "E35.3.3.0", {"start": v(31.26, -3.83) * mm, "end": v(33.38, -3.53) * mm});
            skLineSegment(sketch, "E35.6.3.0", {"start": v(30.67, -2.04) * mm, "end": v(32.57, -1.03) * mm});
            skLineSegment(sketch, "E35.2.4.0", {"start": v(33.65, -7.13) * mm, "end": v(35.18, -8.24) * mm});
            skLineSegment(sketch, "E35.3.4.0", {"start": v(35.18, -8.24) * mm, "end": v(36.72, -6.75) * mm});
            skLineSegment(sketch, "E35.6.4.0", {"start": v(33.65, -7.13) * mm, "end": v(34.6, -5.2) * mm});
            skLineSegment(sketch, "E35.2.5.0", {"start": v(39.06, -9.5) * mm, "end": v(40.94, -9.5) * mm});
            skLineSegment(sketch, "E35.3.5.0", {"start": v(40.94, -9.5) * mm, "end": v(41.32, -7.38) * mm});
            skLineSegment(sketch, "E35.6.5.0", {"start": v(39.06, -9.5) * mm, "end": v(38.68, -7.38) * mm});
            skLineSegment(sketch, "E35.2.6.0", {"start": v(44.82, -8.24) * mm, "end": v(46.35, -7.13) * mm});
            skLineSegment(sketch, "E35.3.6.0", {"start": v(46.35, -7.13) * mm, "end": v(45.4, -5.2) * mm});
            skLineSegment(sketch, "E35.6.6.0", {"start": v(44.82, -8.24) * mm, "end": v(43.28, -6.75) * mm});
            skLineSegment(sketch, "E35.2.7.0", {"start": v(48.74, -3.83) * mm, "end": v(49.33, -2.04) * mm});
            skLineSegment(sketch, "E35.3.7.0", {"start": v(49.33, -2.04) * mm, "end": v(47.43, -1.03) * mm});
            skLineSegment(sketch, "E35.6.7.0", {"start": v(48.74, -3.83) * mm, "end": v(46.62, -3.53) * mm});
            skLineSegment(sketch, "E35.2.8.0", {"start": v(49.33, 2.04) * mm, "end": v(48.74, 3.83) * mm});
            skLineSegment(sketch, "E35.3.8.0", {"start": v(48.74, 3.83) * mm, "end": v(46.62, 3.53) * mm});
            skLineSegment(sketch, "E35.6.8.0", {"start": v(49.33, 2.04) * mm, "end": v(47.43, 1.03) * mm});
            skLineSegment(sketch, "E35.2.9.0", {"start": v(46.35, 7.13) * mm, "end": v(44.82, 8.24) * mm});
            skLineSegment(sketch, "E35.3.9.0", {"start": v(44.82, 8.24) * mm, "end": v(43.28, 6.75) * mm});
            skLineSegment(sketch, "E35.6.9.0", {"start": v(46.35, 7.13) * mm, "end": v(45.4, 5.2) * mm});
            skSolve(sketch);
        }
        {
            var Q0;
            Q0 = qSketchRegion(id + "F16", true);
            extrude(context, id + "F17", {"entities" : qUnion([Q0]), "operationType" : NewBodyOperationType.ADD, "depth" : 4 * mm, "offsetDistance" : 25 * mm});
        }
        {
            var Q0;
            Q0=makeQuery(id+"F17.opExtrude","CAP_FACE",FACE,{"disambiguationData":[OSD([sQuery(id+"F16.wireOp",EDGE,"E29"),sQuery(id+"F16.wireOp",EDGE,"E31"),sQuery(id+"F16.wireOp",EDGE,"E32"),sQuery(id+"F16.wireOp",EDGE,"E33.MirrorCS"),sQuery(id+"F16.wireOp",EDGE,"E34.1.0"),sQuery(id+"F16.wireOp",EDGE,"E34.1.1"),sQuery(id+"F16.wireOp",EDGE,"E34.1.2"),sQuery(id+"F16.wireOp",EDGE,"E34.2.0"),sQuery(id+"F16.wireOp",EDGE,"E34.2.1"),sQuery(id+"F16.wireOp",EDGE,"E34.2.2"),sQuery(id+"F16.wireOp",EDGE,"E35.2.3.0"),sQuery(id+"F16.wireOp",EDGE,"E35.3.3.0"),sQuery(id+"F16.wireOp",EDGE,"E35.6.3.0"),sQuery(id+"F16.wireOp",EDGE,"E35.2.4.0"),sQuery(id+"F16.wireOp",EDGE,"E35.3.4.0"),sQuery(id+"F16.wireOp",EDGE,"E35.6.4.0"),sQuery(id+"F16.wireOp",EDGE,"E35.2.5.0"),sQuery(id+"F16.wireOp",EDGE,"E35.3.5.0"),sQuery(id+"F16.wireOp",EDGE,"E35.6.5.0"),sQuery(id+"F16.wireOp",EDGE,"E35.2.6.0"),sQuery(id+"F16.wireOp",EDGE,"E35.3.6.0"),sQuery(id+"F16.wireOp",EDGE,"E35.6.6.0"),sQuery(id+"F16.wireOp",EDGE,"E35.2.7.0"),sQuery(id+"F16.wireOp",EDGE,"E35.3.7.0"),sQuery(id+"F16.wireOp",EDGE,"E35.6.7.0"),sQuery(id+"F16.wireOp",EDGE,"E35.2.8.0"),sQuery(id+"F16.wireOp",EDGE,"E35.3.8.0"),sQuery(id+"F16.wireOp",EDGE,"E35.6.8.0"),sQuery(id+"F16.wireOp",EDGE,"E35.2.9.0"),sQuery(id+"F16.wireOp",EDGE,"E35.3.9.0"),sQuery(id+"F16.wireOp",EDGE,"E35.6.9.0")])],"isStart":false});
            var sketch = newSketch(context, id + "F18", { "sketchPlane" : qUnion([Q0])});
            skCircle(sketch, "E36.0", {"center": v(40, 0) * mm, "radius": 3 * mm});
            skSolve(sketch);
        }
        {
            var Q0;
            Q0 = qSketchRegion(id + "F18", true);
            extrude(context, id + "F19", {"entities" : qUnion([Q0]), "operationType" : NewBodyOperationType.ADD, "depth" : 2 * mm, "offsetDistance" : 25 * mm});
        }
        {
            var Q0;
            Q0=makeQuery(id+"F19.opExtrude","CAP_FACE",FACE,{"disambiguationData":[OSD([sQuery(id+"F18.wireOp",EDGE,"E36.0")])],"isStart":false});
            var sketch = newSketch(context, id + "F20", { "sketchPlane" : qUnion([Q0])});
            skCircle(sketch, "E37", {"center": v(0, 0) * mm, "radius": 98 * mm});
            skCircle(sketch, "E38.0", {"center": v(0, 0) * mm, "radius": 5 * mm});
            skSolve(sketch);
        }
        {
            var Q0;
            Q0 = qSketchRegion(id + "F20", true);
            extrude(context, id + "F21", {"entities" : qUnion([Q0]), "depth" : 1 * mm, "offsetDistance" : 25 * mm});
        }
        {
            var Q0;
            Q0=makeQuery(id+"F21.opExtrude","SWEPT_BODY",BODY,{"disambiguationData":[OSD([sQuery(id+"F20.wireOp",EDGE,"E37"),sQuery(id+"F20.wireOp",EDGE,"E38.0")])]});
            var Q1;
            Q1=makeQuery(id+"F1.opExtrude","SWEPT_BODY",BODY,{"disambiguationData":[OSD([sQuery(id+"F0.wireOp",EDGE,"E0")])]});
            booleanBodies(context, id + "F22", {"operationType" : BooleanOperationType.SUBTRACTION, "tools" : qUnion([Q0]), "targets" : qUnion([Q1]), "keepTools" : true});
        }
        {
            var Q0;
            Q0=makeQuery(id+"F21.opExtrude","CAP_FACE",FACE,{"disambiguationData":[OSD([sQuery(id+"F20.wireOp",EDGE,"E37"),sQuery(id+"F20.wireOp",EDGE,"E38.0")])],"isStart":true});
            var sketch = newSketch(context, id + "F23", { "sketchPlane" : qUnion([Q0])});
            skCircle(sketch, "E39.0", {"center": v(-40, 0) * mm, "radius": 3 * mm});
            skCircle(sketch, "E40", {"center": v(-40, 0) * mm, "radius": 5 * mm});
            skSolve(sketch);
        }
        {
            var Q0;
            Q0 = qSketchRegion(id + "F23", true);
            extrude(context, id + "F24", {"entities" : qUnion([Q0]), "operationType" : NewBodyOperationType.ADD, "endBound" : BoundingType.UP_TO_NEXT, "depth" : 25 * mm, "offsetDistance" : 25 * mm});
        }
        {
            var Q0;
            Q0=makeQuery(id+"F21.opExtrude","CAP_FACE",FACE,{"disambiguationData":[OSD([sQuery(id+"F20.wireOp",EDGE,"E37"),sQuery(id+"F20.wireOp",EDGE,"E38.0")])],"isStart":false});
            var sketch = newSketch(context, id + "F25", { "sketchPlane" : qUnion([Q0])});
            skLineSegment(sketch, "E41.bottom", {"start": v(1.5, 91) * mm, "end": v(-1.5, 91) * mm});
            skLineSegment(sketch, "E41.top", {"start": v(1.5, 71) * mm, "end": v(-1.5, 71) * mm});
            skLineSegment(sketch, "E41.left", {"start": v(1.5, 91) * mm, "end": v(1.5, 71) * mm});
            skLineSegment(sketch, "E41.right", {"start": v(-1.5, 91) * mm, "end": v(-1.5, 71) * mm});
            skPoint(sketch, "E41.middle", {"position": v(0, 81) * mm});
            skLineSegment(sketch, "E42.1.0", {"start": v(-44.2, 79.56) * mm, "end": v(-34.2, 62.24) * mm});
            skLineSegment(sketch, "E42.1.1", {"start": v(-46.8, 78.06) * mm, "end": v(-36.8, 60.74) * mm});
            skLineSegment(sketch, "E42.1.2", {"start": v(-44.2, 79.56) * mm, "end": v(-46.8, 78.06) * mm});
            skLineSegment(sketch, "E42.1.3", {"start": v(-34.2, 62.24) * mm, "end": v(-36.8, 60.74) * mm});
            skLineSegment(sketch, "E42.2.0", {"start": v(-78.06, 46.8) * mm, "end": v(-60.74, 36.8) * mm});
            skLineSegment(sketch, "E42.2.1", {"start": v(-79.56, 44.2) * mm, "end": v(-62.24, 34.2) * mm});
            skLineSegment(sketch, "E42.2.2", {"start": v(-78.06, 46.8) * mm, "end": v(-79.56, 44.2) * mm});
            skLineSegment(sketch, "E42.2.3", {"start": v(-60.74, 36.8) * mm, "end": v(-62.24, 34.2) * mm});
            skPoint(sketch, "E42.center", {"position": v(0, 0) * mm});
            skLineSegment(sketch, "E43.2.3.0", {"start": v(-91, 1.5) * mm, "end": v(-71, 1.5) * mm});
            skLineSegment(sketch, "E43.3.3.0", {"start": v(-91, -1.5) * mm, "end": v(-71, -1.5) * mm});
            skLineSegment(sketch, "E43.6.3.0", {"start": v(-91, 1.5) * mm, "end": v(-91, -1.5) * mm});
            skLineSegment(sketch, "E43.9.3.0", {"start": v(-71, 1.5) * mm, "end": v(-71, -1.5) * mm});
            skLineSegment(sketch, "E43.2.4.0", {"start": v(-79.56, -44.2) * mm, "end": v(-62.24, -34.2) * mm});
            skLineSegment(sketch, "E43.3.4.0", {"start": v(-78.06, -46.8) * mm, "end": v(-60.74, -36.8) * mm});
            skLineSegment(sketch, "E43.6.4.0", {"start": v(-79.56, -44.2) * mm, "end": v(-78.06, -46.8) * mm});
            skLineSegment(sketch, "E43.9.4.0", {"start": v(-62.24, -34.2) * mm, "end": v(-60.74, -36.8) * mm});
            skLineSegment(sketch, "E43.2.5.0", {"start": v(-46.8, -78.06) * mm, "end": v(-36.8, -60.74) * mm});
            skLineSegment(sketch, "E43.3.5.0", {"start": v(-44.2, -79.56) * mm, "end": v(-34.2, -62.24) * mm});
            skLineSegment(sketch, "E43.6.5.0", {"start": v(-46.8, -78.06) * mm, "end": v(-44.2, -79.56) * mm});
            skLineSegment(sketch, "E43.9.5.0", {"start": v(-36.8, -60.74) * mm, "end": v(-34.2, -62.24) * mm});
            skLineSegment(sketch, "E43.2.6.0", {"start": v(-1.5, -91) * mm, "end": v(-1.5, -71) * mm});
            skLineSegment(sketch, "E43.3.6.0", {"start": v(1.5, -91) * mm, "end": v(1.5, -71) * mm});
            skLineSegment(sketch, "E43.6.6.0", {"start": v(-1.5, -91) * mm, "end": v(1.5, -91) * mm});
            skLineSegment(sketch, "E43.9.6.0", {"start": v(-1.5, -71) * mm, "end": v(1.5, -71) * mm});
            skLineSegment(sketch, "E43.2.7.0", {"start": v(44.2, -79.56) * mm, "end": v(34.2, -62.24) * mm});
            skLineSegment(sketch, "E43.3.7.0", {"start": v(46.8, -78.06) * mm, "end": v(36.8, -60.74) * mm});
            skLineSegment(sketch, "E43.6.7.0", {"start": v(44.2, -79.56) * mm, "end": v(46.8, -78.06) * mm});
            skLineSegment(sketch, "E43.9.7.0", {"start": v(34.2, -62.24) * mm, "end": v(36.8, -60.74) * mm});
            skLineSegment(sketch, "E43.2.8.0", {"start": v(78.06, -46.8) * mm, "end": v(60.74, -36.8) * mm});
            skLineSegment(sketch, "E43.3.8.0", {"start": v(79.56, -44.2) * mm, "end": v(62.24, -34.2) * mm});
            skLineSegment(sketch, "E43.6.8.0", {"start": v(78.06, -46.8) * mm, "end": v(79.56, -44.2) * mm});
            skLineSegment(sketch, "E43.9.8.0", {"start": v(60.74, -36.8) * mm, "end": v(62.24, -34.2) * mm});
            skLineSegment(sketch, "E43.2.9.0", {"start": v(91, -1.5) * mm, "end": v(71, -1.5) * mm});
            skLineSegment(sketch, "E43.3.9.0", {"start": v(91, 1.5) * mm, "end": v(71, 1.5) * mm});
            skLineSegment(sketch, "E43.6.9.0", {"start": v(91, -1.5) * mm, "end": v(91, 1.5) * mm});
            skLineSegment(sketch, "E43.9.9.0", {"start": v(71, -1.5) * mm, "end": v(71, 1.5) * mm});
            skLineSegment(sketch, "E43.2.10.0", {"start": v(79.56, 44.2) * mm, "end": v(62.24, 34.2) * mm});
            skLineSegment(sketch, "E43.3.10.0", {"start": v(78.06, 46.8) * mm, "end": v(60.74, 36.8) * mm});
            skLineSegment(sketch, "E43.6.10.0", {"start": v(79.56, 44.2) * mm, "end": v(78.06, 46.8) * mm});
            skLineSegment(sketch, "E43.9.10.0", {"start": v(62.24, 34.2) * mm, "end": v(60.74, 36.8) * mm});
            skLineSegment(sketch, "E43.2.11.0", {"start": v(46.8, 78.06) * mm, "end": v(36.8, 60.74) * mm});
            skLineSegment(sketch, "E43.3.11.0", {"start": v(44.2, 79.56) * mm, "end": v(34.2, 62.24) * mm});
            skLineSegment(sketch, "E43.6.11.0", {"start": v(46.8, 78.06) * mm, "end": v(44.2, 79.56) * mm});
            skLineSegment(sketch, "E43.9.11.0", {"start": v(36.8, 60.74) * mm, "end": v(34.2, 62.24) * mm});
            skSolve(sketch);
        }
        {
            var Q0;
            Q0 = qSketchRegion(id + "F25", true);
            extrude(context, id + "F26", {"entities" : qUnion([Q0]), "operationType" : NewBodyOperationType.REMOVE, "oppositeDirection" : true, "depth" : 0.5 * mm, "offsetDistance" : 25 * mm});
        }
        {
            var Q0;
            Q0=makeQuery(id+"F21.opExtrude","CAP_FACE",FACE,{"disambiguationData":[OSD([sQuery(id+"F20.wireOp",EDGE,"E37"),sQuery(id+"F20.wireOp",EDGE,"E38.0")])],"isStart":false});
            var sketch = newSketch(context, id + "F27", { "sketchPlane" : qUnion([Q0])});
            skLineSegment(sketch, "E44.bottom", {"start": v(0.75, 90.5) * mm, "end": v(-0.75, 90.5) * mm});
            skLineSegment(sketch, "E44.top", {"start": v(0.75, 78.5) * mm, "end": v(-0.75, 78.5) * mm});
            skLineSegment(sketch, "E44.left", {"start": v(0.75, 90.5) * mm, "end": v(0.75, 78.5) * mm});
            skLineSegment(sketch, "E44.right", {"start": v(-0.75, 90.5) * mm, "end": v(-0.75, 78.5) * mm});
            skPoint(sketch, "E44.middle", {"position": v(0, 84.5) * mm});
            skPoint(sketch, "E44.middle.positionSnap0", {"position": v(0, 71) * mm});
            skPoint(sketch, "E44.centerSnap0", {"position": v(0, 71) * mm});
            skLineSegment(sketch, "E45.1.0", {"start": v(-8.71, 90.08) * mm, "end": v(-10.2, 89.93) * mm});
            skLineSegment(sketch, "E45.1.1", {"start": v(-10.2, 89.93) * mm, "end": v(-8.95, 78) * mm});
            skLineSegment(sketch, "E45.1.2", {"start": v(-8.71, 90.08) * mm, "end": v(-7.46, 78.15) * mm});
            skLineSegment(sketch, "E45.1.3", {"start": v(-7.46, 78.15) * mm, "end": v(-8.95, 78) * mm});
            skLineSegment(sketch, "E45.2.0", {"start": v(-18.08, 88.68) * mm, "end": v(-19.55, 88.37) * mm});
            skLineSegment(sketch, "E45.2.1", {"start": v(-19.55, 88.37) * mm, "end": v(-17.05, 76.63) * mm});
            skLineSegment(sketch, "E45.2.2", {"start": v(-18.08, 88.68) * mm, "end": v(-15.59, 76.94) * mm});
            skLineSegment(sketch, "E45.2.3", {"start": v(-15.59, 76.94) * mm, "end": v(-17.05, 76.63) * mm});
            skPoint(sketch, "E45.center", {"position": v(0, 0) * mm});
            skLineSegment(sketch, "E46.2.3.0", {"start": v(-27.25, 86.3) * mm, "end": v(-28.68, 85.84) * mm});
            skLineSegment(sketch, "E46.3.3.0", {"start": v(-28.68, 85.84) * mm, "end": v(-24.97, 74.43) * mm});
            skLineSegment(sketch, "E46.6.3.0", {"start": v(-27.25, 86.3) * mm, "end": v(-23.54, 74.89) * mm});
            skLineSegment(sketch, "E46.9.3.0", {"start": v(-23.54, 74.89) * mm, "end": v(-24.97, 74.43) * mm});
            skLineSegment(sketch, "E46.2.4.0", {"start": v(-36.12, 82.98) * mm, "end": v(-37.5, 82.37) * mm});
            skLineSegment(sketch, "E46.3.4.0", {"start": v(-37.5, 82.37) * mm, "end": v(-32.61, 71.4) * mm});
            skLineSegment(sketch, "E46.6.4.0", {"start": v(-36.12, 82.98) * mm, "end": v(-31.24, 72.02) * mm});
            skLineSegment(sketch, "E46.9.4.0", {"start": v(-31.24, 72.02) * mm, "end": v(-32.61, 71.4) * mm});
            skLineSegment(sketch, "E46.2.5.0", {"start": v(-44.6, 78.75) * mm, "end": v(-45.9, 78) * mm});
            skLineSegment(sketch, "E46.3.5.0", {"start": v(-45.9, 78) * mm, "end": v(-39.9, 67.6) * mm});
            skLineSegment(sketch, "E46.6.5.0", {"start": v(-44.6, 78.75) * mm, "end": v(-38.6, 68.36) * mm});
            skLineSegment(sketch, "E46.9.5.0", {"start": v(-38.6, 68.36) * mm, "end": v(-39.9, 67.6) * mm});
            skLineSegment(sketch, "E46.2.6.0", {"start": v(-52.59, 73.66) * mm, "end": v(-53.8, 72.78) * mm});
            skLineSegment(sketch, "E46.3.6.0", {"start": v(-53.8, 72.78) * mm, "end": v(-46.75, 63.07) * mm});
            skLineSegment(sketch, "E46.6.6.0", {"start": v(-52.59, 73.66) * mm, "end": v(-45.53, 63.95) * mm});
            skLineSegment(sketch, "E46.9.6.0", {"start": v(-45.53, 63.95) * mm, "end": v(-46.75, 63.07) * mm});
            skLineSegment(sketch, "E46.2.7.0", {"start": v(-60, 67.76) * mm, "end": v(-61.11, 66.75) * mm});
            skLineSegment(sketch, "E46.3.7.0", {"start": v(-61.11, 66.75) * mm, "end": v(-53.08, 57.84) * mm});
            skLineSegment(sketch, "E46.6.7.0", {"start": v(-60, 67.76) * mm, "end": v(-51.97, 58.84) * mm});
            skLineSegment(sketch, "E46.9.7.0", {"start": v(-51.97, 58.84) * mm, "end": v(-53.08, 57.84) * mm});
            skLineSegment(sketch, "E46.2.8.0", {"start": v(-66.75, 61.11) * mm, "end": v(-67.76, 60) * mm});
            skLineSegment(sketch, "E46.3.8.0", {"start": v(-67.76, 60) * mm, "end": v(-58.84, 51.97) * mm});
            skLineSegment(sketch, "E46.6.8.0", {"start": v(-66.75, 61.11) * mm, "end": v(-57.84, 53.08) * mm});
            skLineSegment(sketch, "E46.9.8.0", {"start": v(-57.84, 53.08) * mm, "end": v(-58.84, 51.97) * mm});
            skLineSegment(sketch, "E46.2.9.0", {"start": v(-72.78, 53.8) * mm, "end": v(-73.66, 52.59) * mm});
            skLineSegment(sketch, "E46.3.9.0", {"start": v(-73.66, 52.59) * mm, "end": v(-63.95, 45.53) * mm});
            skLineSegment(sketch, "E46.6.9.0", {"start": v(-72.78, 53.8) * mm, "end": v(-63.07, 46.75) * mm});
            skLineSegment(sketch, "E46.9.9.0", {"start": v(-63.07, 46.75) * mm, "end": v(-63.95, 45.53) * mm});
            skLineSegment(sketch, "E46.2.10.0", {"start": v(-78, 45.9) * mm, "end": v(-78.75, 44.6) * mm});
            skLineSegment(sketch, "E46.3.10.0", {"start": v(-78.75, 44.6) * mm, "end": v(-68.36, 38.6) * mm});
            skLineSegment(sketch, "E46.6.10.0", {"start": v(-78, 45.9) * mm, "end": v(-67.6, 39.9) * mm});
            skLineSegment(sketch, "E46.9.10.0", {"start": v(-67.6, 39.9) * mm, "end": v(-68.36, 38.6) * mm});
            skLineSegment(sketch, "E46.2.11.0", {"start": v(-82.37, 37.5) * mm, "end": v(-82.98, 36.12) * mm});
            skLineSegment(sketch, "E46.3.11.0", {"start": v(-82.98, 36.12) * mm, "end": v(-72.02, 31.24) * mm});
            skLineSegment(sketch, "E46.6.11.0", {"start": v(-82.37, 37.5) * mm, "end": v(-71.4, 32.61) * mm});
            skLineSegment(sketch, "E46.9.11.0", {"start": v(-71.4, 32.61) * mm, "end": v(-72.02, 31.24) * mm});
            skLineSegment(sketch, "E46.2.12.0", {"start": v(-85.84, 28.68) * mm, "end": v(-86.3, 27.25) * mm});
            skLineSegment(sketch, "E46.3.12.0", {"start": v(-86.3, 27.25) * mm, "end": v(-74.89, 23.54) * mm});
            skLineSegment(sketch, "E46.6.12.0", {"start": v(-85.84, 28.68) * mm, "end": v(-74.43, 24.97) * mm});
            skLineSegment(sketch, "E46.9.12.0", {"start": v(-74.43, 24.97) * mm, "end": v(-74.89, 23.54) * mm});
            skLineSegment(sketch, "E46.2.13.0", {"start": v(-88.37, 19.55) * mm, "end": v(-88.68, 18.08) * mm});
            skLineSegment(sketch, "E46.3.13.0", {"start": v(-88.68, 18.08) * mm, "end": v(-76.94, 15.59) * mm});
            skLineSegment(sketch, "E46.6.13.0", {"start": v(-88.37, 19.55) * mm, "end": v(-76.63, 17.05) * mm});
            skLineSegment(sketch, "E46.9.13.0", {"start": v(-76.63, 17.05) * mm, "end": v(-76.94, 15.59) * mm});
            skLineSegment(sketch, "E46.2.14.0", {"start": v(-89.93, 10.2) * mm, "end": v(-90.08, 8.71) * mm});
            skLineSegment(sketch, "E46.3.14.0", {"start": v(-90.08, 8.71) * mm, "end": v(-78.15, 7.46) * mm});
            skLineSegment(sketch, "E46.6.14.0", {"start": v(-89.93, 10.2) * mm, "end": v(-78, 8.95) * mm});
            skLineSegment(sketch, "E46.9.14.0", {"start": v(-78, 8.95) * mm, "end": v(-78.15, 7.46) * mm});
            skLineSegment(sketch, "E46.2.15.0", {"start": v(-90.5, 0.75) * mm, "end": v(-90.5, -0.75) * mm});
            skLineSegment(sketch, "E46.3.15.0", {"start": v(-90.5, -0.75) * mm, "end": v(-78.5, -0.75) * mm});
            skLineSegment(sketch, "E46.6.15.0", {"start": v(-90.5, 0.75) * mm, "end": v(-78.5, 0.75) * mm});
            skLineSegment(sketch, "E46.9.15.0", {"start": v(-78.5, 0.75) * mm, "end": v(-78.5, -0.75) * mm});
            skLineSegment(sketch, "E46.2.16.0", {"start": v(-90.08, -8.71) * mm, "end": v(-89.93, -10.2) * mm});
            skLineSegment(sketch, "E46.3.16.0", {"start": v(-89.93, -10.2) * mm, "end": v(-78, -8.95) * mm});
            skLineSegment(sketch, "E46.6.16.0", {"start": v(-90.08, -8.71) * mm, "end": v(-78.15, -7.46) * mm});
            skLineSegment(sketch, "E46.9.16.0", {"start": v(-78.15, -7.46) * mm, "end": v(-78, -8.95) * mm});
            skLineSegment(sketch, "E46.2.17.0", {"start": v(-88.68, -18.08) * mm, "end": v(-88.37, -19.55) * mm});
            skLineSegment(sketch, "E46.3.17.0", {"start": v(-88.37, -19.55) * mm, "end": v(-76.63, -17.05) * mm});
            skLineSegment(sketch, "E46.6.17.0", {"start": v(-88.68, -18.08) * mm, "end": v(-76.94, -15.59) * mm});
            skLineSegment(sketch, "E46.9.17.0", {"start": v(-76.94, -15.59) * mm, "end": v(-76.63, -17.05) * mm});
            skLineSegment(sketch, "E46.2.18.0", {"start": v(-86.3, -27.25) * mm, "end": v(-85.84, -28.68) * mm});
            skLineSegment(sketch, "E46.3.18.0", {"start": v(-85.84, -28.68) * mm, "end": v(-74.43, -24.97) * mm});
            skLineSegment(sketch, "E46.6.18.0", {"start": v(-86.3, -27.25) * mm, "end": v(-74.89, -23.54) * mm});
            skLineSegment(sketch, "E46.9.18.0", {"start": v(-74.89, -23.54) * mm, "end": v(-74.43, -24.97) * mm});
            skLineSegment(sketch, "E46.2.19.0", {"start": v(-82.98, -36.12) * mm, "end": v(-82.37, -37.5) * mm});
            skLineSegment(sketch, "E46.3.19.0", {"start": v(-82.37, -37.5) * mm, "end": v(-71.4, -32.61) * mm});
            skLineSegment(sketch, "E46.6.19.0", {"start": v(-82.98, -36.12) * mm, "end": v(-72.02, -31.24) * mm});
            skLineSegment(sketch, "E46.9.19.0", {"start": v(-72.02, -31.24) * mm, "end": v(-71.4, -32.61) * mm});
            skLineSegment(sketch, "E46.2.20.0", {"start": v(-78.75, -44.6) * mm, "end": v(-78, -45.9) * mm});
            skLineSegment(sketch, "E46.3.20.0", {"start": v(-78, -45.9) * mm, "end": v(-67.6, -39.9) * mm});
            skLineSegment(sketch, "E46.6.20.0", {"start": v(-78.75, -44.6) * mm, "end": v(-68.36, -38.6) * mm});
            skLineSegment(sketch, "E46.9.20.0", {"start": v(-68.36, -38.6) * mm, "end": v(-67.6, -39.9) * mm});
            skLineSegment(sketch, "E46.2.21.0", {"start": v(-73.66, -52.59) * mm, "end": v(-72.78, -53.8) * mm});
            skLineSegment(sketch, "E46.3.21.0", {"start": v(-72.78, -53.8) * mm, "end": v(-63.07, -46.75) * mm});
            skLineSegment(sketch, "E46.6.21.0", {"start": v(-73.66, -52.59) * mm, "end": v(-63.95, -45.53) * mm});
            skLineSegment(sketch, "E46.9.21.0", {"start": v(-63.95, -45.53) * mm, "end": v(-63.07, -46.75) * mm});
            skLineSegment(sketch, "E46.2.22.0", {"start": v(-67.76, -60) * mm, "end": v(-66.75, -61.11) * mm});
            skLineSegment(sketch, "E46.3.22.0", {"start": v(-66.75, -61.11) * mm, "end": v(-57.84, -53.08) * mm});
            skLineSegment(sketch, "E46.6.22.0", {"start": v(-67.76, -60) * mm, "end": v(-58.84, -51.97) * mm});
            skLineSegment(sketch, "E46.9.22.0", {"start": v(-58.84, -51.97) * mm, "end": v(-57.84, -53.08) * mm});
            skLineSegment(sketch, "E46.2.23.0", {"start": v(-61.11, -66.75) * mm, "end": v(-60, -67.76) * mm});
            skLineSegment(sketch, "E46.3.23.0", {"start": v(-60, -67.76) * mm, "end": v(-51.97, -58.84) * mm});
            skLineSegment(sketch, "E46.6.23.0", {"start": v(-61.11, -66.75) * mm, "end": v(-53.08, -57.84) * mm});
            skLineSegment(sketch, "E46.9.23.0", {"start": v(-53.08, -57.84) * mm, "end": v(-51.97, -58.84) * mm});
            skLineSegment(sketch, "E46.2.24.0", {"start": v(-53.8, -72.78) * mm, "end": v(-52.59, -73.66) * mm});
            skLineSegment(sketch, "E46.3.24.0", {"start": v(-52.59, -73.66) * mm, "end": v(-45.53, -63.95) * mm});
            skLineSegment(sketch, "E46.6.24.0", {"start": v(-53.8, -72.78) * mm, "end": v(-46.75, -63.07) * mm});
            skLineSegment(sketch, "E46.9.24.0", {"start": v(-46.75, -63.07) * mm, "end": v(-45.53, -63.95) * mm});
            skLineSegment(sketch, "E46.2.25.0", {"start": v(-45.9, -78) * mm, "end": v(-44.6, -78.75) * mm});
            skLineSegment(sketch, "E46.3.25.0", {"start": v(-44.6, -78.75) * mm, "end": v(-38.6, -68.36) * mm});
            skLineSegment(sketch, "E46.6.25.0", {"start": v(-45.9, -78) * mm, "end": v(-39.9, -67.6) * mm});
            skLineSegment(sketch, "E46.9.25.0", {"start": v(-39.9, -67.6) * mm, "end": v(-38.6, -68.36) * mm});
            skLineSegment(sketch, "E46.2.26.0", {"start": v(-37.5, -82.37) * mm, "end": v(-36.12, -82.98) * mm});
            skLineSegment(sketch, "E46.3.26.0", {"start": v(-36.12, -82.98) * mm, "end": v(-31.24, -72.02) * mm});
            skLineSegment(sketch, "E46.6.26.0", {"start": v(-37.5, -82.37) * mm, "end": v(-32.61, -71.4) * mm});
            skLineSegment(sketch, "E46.9.26.0", {"start": v(-32.61, -71.4) * mm, "end": v(-31.24, -72.02) * mm});
            skLineSegment(sketch, "E46.2.27.0", {"start": v(-28.68, -85.84) * mm, "end": v(-27.25, -86.3) * mm});
            skLineSegment(sketch, "E46.3.27.0", {"start": v(-27.25, -86.3) * mm, "end": v(-23.54, -74.89) * mm});
            skLineSegment(sketch, "E46.6.27.0", {"start": v(-28.68, -85.84) * mm, "end": v(-24.97, -74.43) * mm});
            skLineSegment(sketch, "E46.9.27.0", {"start": v(-24.97, -74.43) * mm, "end": v(-23.54, -74.89) * mm});
            skLineSegment(sketch, "E46.2.28.0", {"start": v(-19.55, -88.37) * mm, "end": v(-18.08, -88.68) * mm});
            skLineSegment(sketch, "E46.3.28.0", {"start": v(-18.08, -88.68) * mm, "end": v(-15.59, -76.94) * mm});
            skLineSegment(sketch, "E46.6.28.0", {"start": v(-19.55, -88.37) * mm, "end": v(-17.05, -76.63) * mm});
            skLineSegment(sketch, "E46.9.28.0", {"start": v(-17.05, -76.63) * mm, "end": v(-15.59, -76.94) * mm});
            skLineSegment(sketch, "E46.2.29.0", {"start": v(-10.2, -89.93) * mm, "end": v(-8.71, -90.08) * mm});
            skLineSegment(sketch, "E46.3.29.0", {"start": v(-8.71, -90.08) * mm, "end": v(-7.46, -78.15) * mm});
            skLineSegment(sketch, "E46.6.29.0", {"start": v(-10.2, -89.93) * mm, "end": v(-8.95, -78) * mm});
            skLineSegment(sketch, "E46.9.29.0", {"start": v(-8.95, -78) * mm, "end": v(-7.46, -78.15) * mm});
            skLineSegment(sketch, "E46.2.30.0", {"start": v(-0.75, -90.5) * mm, "end": v(0.75, -90.5) * mm});
            skLineSegment(sketch, "E46.3.30.0", {"start": v(0.75, -90.5) * mm, "end": v(0.75, -78.5) * mm});
            skLineSegment(sketch, "E46.6.30.0", {"start": v(-0.75, -90.5) * mm, "end": v(-0.75, -78.5) * mm});
            skLineSegment(sketch, "E46.9.30.0", {"start": v(-0.75, -78.5) * mm, "end": v(0.75, -78.5) * mm});
            skLineSegment(sketch, "E46.2.31.0", {"start": v(8.71, -90.08) * mm, "end": v(10.2, -89.93) * mm});
            skLineSegment(sketch, "E46.3.31.0", {"start": v(10.2, -89.93) * mm, "end": v(8.95, -78) * mm});
            skLineSegment(sketch, "E46.6.31.0", {"start": v(8.71, -90.08) * mm, "end": v(7.46, -78.15) * mm});
            skLineSegment(sketch, "E46.9.31.0", {"start": v(7.46, -78.15) * mm, "end": v(8.95, -78) * mm});
            skLineSegment(sketch, "E46.2.32.0", {"start": v(18.08, -88.68) * mm, "end": v(19.55, -88.37) * mm});
            skLineSegment(sketch, "E46.3.32.0", {"start": v(19.55, -88.37) * mm, "end": v(17.05, -76.63) * mm});
            skLineSegment(sketch, "E46.6.32.0", {"start": v(18.08, -88.68) * mm, "end": v(15.59, -76.94) * mm});
            skLineSegment(sketch, "E46.9.32.0", {"start": v(15.59, -76.94) * mm, "end": v(17.05, -76.63) * mm});
            skLineSegment(sketch, "E46.2.33.0", {"start": v(27.25, -86.3) * mm, "end": v(28.68, -85.84) * mm});
            skLineSegment(sketch, "E46.3.33.0", {"start": v(28.68, -85.84) * mm, "end": v(24.97, -74.43) * mm});
            skLineSegment(sketch, "E46.6.33.0", {"start": v(27.25, -86.3) * mm, "end": v(23.54, -74.89) * mm});
            skLineSegment(sketch, "E46.9.33.0", {"start": v(23.54, -74.89) * mm, "end": v(24.97, -74.43) * mm});
            skLineSegment(sketch, "E46.2.34.0", {"start": v(36.12, -82.98) * mm, "end": v(37.5, -82.37) * mm});
            skLineSegment(sketch, "E46.3.34.0", {"start": v(37.5, -82.37) * mm, "end": v(32.61, -71.4) * mm});
            skLineSegment(sketch, "E46.6.34.0", {"start": v(36.12, -82.98) * mm, "end": v(31.24, -72.02) * mm});
            skLineSegment(sketch, "E46.9.34.0", {"start": v(31.24, -72.02) * mm, "end": v(32.61, -71.4) * mm});
            skLineSegment(sketch, "E46.2.35.0", {"start": v(44.6, -78.75) * mm, "end": v(45.9, -78) * mm});
            skLineSegment(sketch, "E46.3.35.0", {"start": v(45.9, -78) * mm, "end": v(39.9, -67.6) * mm});
            skLineSegment(sketch, "E46.6.35.0", {"start": v(44.6, -78.75) * mm, "end": v(38.6, -68.36) * mm});
            skLineSegment(sketch, "E46.9.35.0", {"start": v(38.6, -68.36) * mm, "end": v(39.9, -67.6) * mm});
            skLineSegment(sketch, "E46.2.36.0", {"start": v(52.59, -73.66) * mm, "end": v(53.8, -72.78) * mm});
            skLineSegment(sketch, "E46.3.36.0", {"start": v(53.8, -72.78) * mm, "end": v(46.75, -63.07) * mm});
            skLineSegment(sketch, "E46.6.36.0", {"start": v(52.59, -73.66) * mm, "end": v(45.53, -63.95) * mm});
            skLineSegment(sketch, "E46.9.36.0", {"start": v(45.53, -63.95) * mm, "end": v(46.75, -63.07) * mm});
            skLineSegment(sketch, "E46.2.37.0", {"start": v(60, -67.76) * mm, "end": v(61.11, -66.75) * mm});
            skLineSegment(sketch, "E46.3.37.0", {"start": v(61.11, -66.75) * mm, "end": v(53.08, -57.84) * mm});
            skLineSegment(sketch, "E46.6.37.0", {"start": v(60, -67.76) * mm, "end": v(51.97, -58.84) * mm});
            skLineSegment(sketch, "E46.9.37.0", {"start": v(51.97, -58.84) * mm, "end": v(53.08, -57.84) * mm});
            skLineSegment(sketch, "E46.2.38.0", {"start": v(66.75, -61.11) * mm, "end": v(67.76, -60) * mm});
            skLineSegment(sketch, "E46.3.38.0", {"start": v(67.76, -60) * mm, "end": v(58.84, -51.97) * mm});
            skLineSegment(sketch, "E46.6.38.0", {"start": v(66.75, -61.11) * mm, "end": v(57.84, -53.08) * mm});
            skLineSegment(sketch, "E46.9.38.0", {"start": v(57.84, -53.08) * mm, "end": v(58.84, -51.97) * mm});
            skLineSegment(sketch, "E46.2.39.0", {"start": v(72.78, -53.8) * mm, "end": v(73.66, -52.59) * mm});
            skLineSegment(sketch, "E46.3.39.0", {"start": v(73.66, -52.59) * mm, "end": v(63.95, -45.53) * mm});
            skLineSegment(sketch, "E46.6.39.0", {"start": v(72.78, -53.8) * mm, "end": v(63.07, -46.75) * mm});
            skLineSegment(sketch, "E46.9.39.0", {"start": v(63.07, -46.75) * mm, "end": v(63.95, -45.53) * mm});
            skLineSegment(sketch, "E46.2.40.0", {"start": v(78, -45.9) * mm, "end": v(78.75, -44.6) * mm});
            skLineSegment(sketch, "E46.3.40.0", {"start": v(78.75, -44.6) * mm, "end": v(68.36, -38.6) * mm});
            skLineSegment(sketch, "E46.6.40.0", {"start": v(78, -45.9) * mm, "end": v(67.6, -39.9) * mm});
            skLineSegment(sketch, "E46.9.40.0", {"start": v(67.6, -39.9) * mm, "end": v(68.36, -38.6) * mm});
            skLineSegment(sketch, "E46.2.41.0", {"start": v(82.37, -37.5) * mm, "end": v(82.98, -36.12) * mm});
            skLineSegment(sketch, "E46.3.41.0", {"start": v(82.98, -36.12) * mm, "end": v(72.02, -31.24) * mm});
            skLineSegment(sketch, "E46.6.41.0", {"start": v(82.37, -37.5) * mm, "end": v(71.4, -32.61) * mm});
            skLineSegment(sketch, "E46.9.41.0", {"start": v(71.4, -32.61) * mm, "end": v(72.02, -31.24) * mm});
            skLineSegment(sketch, "E46.2.42.0", {"start": v(85.84, -28.68) * mm, "end": v(86.3, -27.25) * mm});
            skLineSegment(sketch, "E46.3.42.0", {"start": v(86.3, -27.25) * mm, "end": v(74.89, -23.54) * mm});
            skLineSegment(sketch, "E46.6.42.0", {"start": v(85.84, -28.68) * mm, "end": v(74.43, -24.97) * mm});
            skLineSegment(sketch, "E46.9.42.0", {"start": v(74.43, -24.97) * mm, "end": v(74.89, -23.54) * mm});
            skLineSegment(sketch, "E46.2.43.0", {"start": v(88.37, -19.55) * mm, "end": v(88.68, -18.08) * mm});
            skLineSegment(sketch, "E46.3.43.0", {"start": v(88.68, -18.08) * mm, "end": v(76.94, -15.59) * mm});
            skLineSegment(sketch, "E46.6.43.0", {"start": v(88.37, -19.55) * mm, "end": v(76.63, -17.05) * mm});
            skLineSegment(sketch, "E46.9.43.0", {"start": v(76.63, -17.05) * mm, "end": v(76.94, -15.59) * mm});
            skLineSegment(sketch, "E46.2.44.0", {"start": v(89.93, -10.2) * mm, "end": v(90.08, -8.71) * mm});
            skLineSegment(sketch, "E46.3.44.0", {"start": v(90.08, -8.71) * mm, "end": v(78.15, -7.46) * mm});
            skLineSegment(sketch, "E46.6.44.0", {"start": v(89.93, -10.2) * mm, "end": v(78, -8.95) * mm});
            skLineSegment(sketch, "E46.9.44.0", {"start": v(78, -8.95) * mm, "end": v(78.15, -7.46) * mm});
            skLineSegment(sketch, "E46.2.45.0", {"start": v(90.5, -0.75) * mm, "end": v(90.5, 0.75) * mm});
            skLineSegment(sketch, "E46.3.45.0", {"start": v(90.5, 0.75) * mm, "end": v(78.5, 0.75) * mm});
            skLineSegment(sketch, "E46.6.45.0", {"start": v(90.5, -0.75) * mm, "end": v(78.5, -0.75) * mm});
            skLineSegment(sketch, "E46.9.45.0", {"start": v(78.5, -0.75) * mm, "end": v(78.5, 0.75) * mm});
            skLineSegment(sketch, "E46.2.46.0", {"start": v(90.08, 8.71) * mm, "end": v(89.93, 10.2) * mm});
            skLineSegment(sketch, "E46.3.46.0", {"start": v(89.93, 10.2) * mm, "end": v(78, 8.95) * mm});
            skLineSegment(sketch, "E46.6.46.0", {"start": v(90.08, 8.71) * mm, "end": v(78.15, 7.46) * mm});
            skLineSegment(sketch, "E46.9.46.0", {"start": v(78.15, 7.46) * mm, "end": v(78, 8.95) * mm});
            skLineSegment(sketch, "E46.2.47.0", {"start": v(88.68, 18.08) * mm, "end": v(88.37, 19.55) * mm});
            skLineSegment(sketch, "E46.3.47.0", {"start": v(88.37, 19.55) * mm, "end": v(76.63, 17.05) * mm});
            skLineSegment(sketch, "E46.6.47.0", {"start": v(88.68, 18.08) * mm, "end": v(76.94, 15.59) * mm});
            skLineSegment(sketch, "E46.9.47.0", {"start": v(76.94, 15.59) * mm, "end": v(76.63, 17.05) * mm});
            skLineSegment(sketch, "E46.2.48.0", {"start": v(86.3, 27.25) * mm, "end": v(85.84, 28.68) * mm});
            skLineSegment(sketch, "E46.3.48.0", {"start": v(85.84, 28.68) * mm, "end": v(74.43, 24.97) * mm});
            skLineSegment(sketch, "E46.6.48.0", {"start": v(86.3, 27.25) * mm, "end": v(74.89, 23.54) * mm});
            skLineSegment(sketch, "E46.9.48.0", {"start": v(74.89, 23.54) * mm, "end": v(74.43, 24.97) * mm});
            skLineSegment(sketch, "E46.2.49.0", {"start": v(82.98, 36.12) * mm, "end": v(82.37, 37.5) * mm});
            skLineSegment(sketch, "E46.3.49.0", {"start": v(82.37, 37.5) * mm, "end": v(71.4, 32.61) * mm});
            skLineSegment(sketch, "E46.6.49.0", {"start": v(82.98, 36.12) * mm, "end": v(72.02, 31.24) * mm});
            skLineSegment(sketch, "E46.9.49.0", {"start": v(72.02, 31.24) * mm, "end": v(71.4, 32.61) * mm});
            skLineSegment(sketch, "E46.2.50.0", {"start": v(78.75, 44.6) * mm, "end": v(78, 45.9) * mm});
            skLineSegment(sketch, "E46.3.50.0", {"start": v(78, 45.9) * mm, "end": v(67.6, 39.9) * mm});
            skLineSegment(sketch, "E46.6.50.0", {"start": v(78.75, 44.6) * mm, "end": v(68.36, 38.6) * mm});
            skLineSegment(sketch, "E46.9.50.0", {"start": v(68.36, 38.6) * mm, "end": v(67.6, 39.9) * mm});
            skLineSegment(sketch, "E46.2.51.0", {"start": v(73.66, 52.59) * mm, "end": v(72.78, 53.8) * mm});
            skLineSegment(sketch, "E46.3.51.0", {"start": v(72.78, 53.8) * mm, "end": v(63.07, 46.75) * mm});
            skLineSegment(sketch, "E46.6.51.0", {"start": v(73.66, 52.59) * mm, "end": v(63.95, 45.53) * mm});
            skLineSegment(sketch, "E46.9.51.0", {"start": v(63.95, 45.53) * mm, "end": v(63.07, 46.75) * mm});
            skLineSegment(sketch, "E46.2.52.0", {"start": v(67.76, 60) * mm, "end": v(66.75, 61.11) * mm});
            skLineSegment(sketch, "E46.3.52.0", {"start": v(66.75, 61.11) * mm, "end": v(57.84, 53.08) * mm});
            skLineSegment(sketch, "E46.6.52.0", {"start": v(67.76, 60) * mm, "end": v(58.84, 51.97) * mm});
            skLineSegment(sketch, "E46.9.52.0", {"start": v(58.84, 51.97) * mm, "end": v(57.84, 53.08) * mm});
            skLineSegment(sketch, "E46.2.53.0", {"start": v(61.11, 66.75) * mm, "end": v(60, 67.76) * mm});
            skLineSegment(sketch, "E46.3.53.0", {"start": v(60, 67.76) * mm, "end": v(51.97, 58.84) * mm});
            skLineSegment(sketch, "E46.6.53.0", {"start": v(61.11, 66.75) * mm, "end": v(53.08, 57.84) * mm});
            skLineSegment(sketch, "E46.9.53.0", {"start": v(53.08, 57.84) * mm, "end": v(51.97, 58.84) * mm});
            skLineSegment(sketch, "E46.2.54.0", {"start": v(53.8, 72.78) * mm, "end": v(52.59, 73.66) * mm});
            skLineSegment(sketch, "E46.3.54.0", {"start": v(52.59, 73.66) * mm, "end": v(45.53, 63.95) * mm});
            skLineSegment(sketch, "E46.6.54.0", {"start": v(53.8, 72.78) * mm, "end": v(46.75, 63.07) * mm});
            skLineSegment(sketch, "E46.9.54.0", {"start": v(46.75, 63.07) * mm, "end": v(45.53, 63.95) * mm});
            skLineSegment(sketch, "E46.2.55.0", {"start": v(45.9, 78) * mm, "end": v(44.6, 78.75) * mm});
            skLineSegment(sketch, "E46.3.55.0", {"start": v(44.6, 78.75) * mm, "end": v(38.6, 68.36) * mm});
            skLineSegment(sketch, "E46.6.55.0", {"start": v(45.9, 78) * mm, "end": v(39.9, 67.6) * mm});
            skLineSegment(sketch, "E46.9.55.0", {"start": v(39.9, 67.6) * mm, "end": v(38.6, 68.36) * mm});
            skLineSegment(sketch, "E46.2.56.0", {"start": v(37.5, 82.37) * mm, "end": v(36.12, 82.98) * mm});
            skLineSegment(sketch, "E46.3.56.0", {"start": v(36.12, 82.98) * mm, "end": v(31.24, 72.02) * mm});
            skLineSegment(sketch, "E46.6.56.0", {"start": v(37.5, 82.37) * mm, "end": v(32.61, 71.4) * mm});
            skLineSegment(sketch, "E46.9.56.0", {"start": v(32.61, 71.4) * mm, "end": v(31.24, 72.02) * mm});
            skLineSegment(sketch, "E46.2.57.0", {"start": v(28.68, 85.84) * mm, "end": v(27.25, 86.3) * mm});
            skLineSegment(sketch, "E46.3.57.0", {"start": v(27.25, 86.3) * mm, "end": v(23.54, 74.89) * mm});
            skLineSegment(sketch, "E46.6.57.0", {"start": v(28.68, 85.84) * mm, "end": v(24.97, 74.43) * mm});
            skLineSegment(sketch, "E46.9.57.0", {"start": v(24.97, 74.43) * mm, "end": v(23.54, 74.89) * mm});
            skLineSegment(sketch, "E46.2.58.0", {"start": v(19.55, 88.37) * mm, "end": v(18.08, 88.68) * mm});
            skLineSegment(sketch, "E46.3.58.0", {"start": v(18.08, 88.68) * mm, "end": v(15.59, 76.94) * mm});
            skLineSegment(sketch, "E46.6.58.0", {"start": v(19.55, 88.37) * mm, "end": v(17.05, 76.63) * mm});
            skLineSegment(sketch, "E46.9.58.0", {"start": v(17.05, 76.63) * mm, "end": v(15.59, 76.94) * mm});
            skLineSegment(sketch, "E46.2.59.0", {"start": v(10.2, 89.93) * mm, "end": v(8.71, 90.08) * mm});
            skLineSegment(sketch, "E46.3.59.0", {"start": v(8.71, 90.08) * mm, "end": v(7.46, 78.15) * mm});
            skLineSegment(sketch, "E46.6.59.0", {"start": v(10.2, 89.93) * mm, "end": v(8.95, 78) * mm});
            skLineSegment(sketch, "E46.9.59.0", {"start": v(8.95, 78) * mm, "end": v(7.46, 78.15) * mm});
            skSolve(sketch);
        }
        {
            var Q0;
            Q0 = qSketchRegion(id + "F27", true);
            extrude(context, id + "F28", {"entities" : qUnion([Q0]), "operationType" : NewBodyOperationType.REMOVE, "oppositeDirection" : true, "depth" : .2 * mm, "offsetDistance" : 25 * mm});
        }
        {
            var Q0;
            Q0=makeQuery(id+"F26.boolean.opBoolean","COPY",FACE,{"derivedFrom":makeQuery(id+"F26.opExtrude","CAP_FACE",FACE,{"disambiguationData":[OSD([sQuery(id+"F25.wireOp",EDGE,"E41.bottom"),sQuery(id+"F25.wireOp",EDGE,"E41.top"),sQuery(id+"F25.wireOp",EDGE,"E41.left"),sQuery(id+"F25.wireOp",EDGE,"E41.right")])],"isStart":false})});
            extrude(context, id + "F29", {"entities" : qUnion([Q0]), "depth" : 1 * mm, "offsetDistance" : 25 * mm});
        }
        {
            var Q0;
            Q0=makeQuery(id+"F28.boolean.opBoolean","COPY",FACE,{"derivedFrom":makeQuery(id+"F28.opExtrude","CAP_FACE",FACE,{"disambiguationData":[OSD([sQuery(id+"F27.wireOp",EDGE,"E46.2.59.0"),sQuery(id+"F27.wireOp",EDGE,"E46.3.59.0"),sQuery(id+"F27.wireOp",EDGE,"E46.6.59.0"),sQuery(id+"F27.wireOp",EDGE,"E46.9.59.0")])],"isStart":false})});
            extrude(context, id + "F30", {"entities" : qUnion([Q0]), "depth" : 0.4 * mm, "offsetDistance" : 25 * mm});
        }
        {
            var Q0;
            Q0=makeQuery(id+"F15.opExtrude","CAP_FACE",FACE,{"disambiguationData":[OSD([sQuery(id+"F14.wireOp",EDGE,"E21.0"),sQuery(id+"F14.wireOp",EDGE,"E22"),sQuery(id+"F14.wireOp",EDGE,"E23"),sQuery(id+"F14.wireOp",EDGE,"E24"),sQuery(id+"F14.wireOp",EDGE,"E25.MirrorCS"),sQuery(id+"F14.wireOp",EDGE,"E26.MirrorCS"),sQuery(id+"F14.wireOp",EDGE,"E27.1.0"),sQuery(id+"F14.wireOp",EDGE,"E27.1.1"),sQuery(id+"F14.wireOp",EDGE,"E27.1.2"),sQuery(id+"F14.wireOp",EDGE,"E27.1.3"),sQuery(id+"F14.wireOp",EDGE,"E27.2.0"),sQuery(id+"F14.wireOp",EDGE,"E27.2.1"),sQuery(id+"F14.wireOp",EDGE,"E27.2.2"),sQuery(id+"F14.wireOp",EDGE,"E27.2.3"),sQuery(id+"F14.wireOp",EDGE,"E28.1.3.0"),sQuery(id+"F14.wireOp",EDGE,"E28.3.3.0"),sQuery(id+"F14.wireOp",EDGE,"E28.6.3.0"),sQuery(id+"F14.wireOp",EDGE,"E28.9.3.0"),sQuery(id+"F14.wireOp",EDGE,"E28.1.4.0"),sQuery(id+"F14.wireOp",EDGE,"E28.3.4.0"),sQuery(id+"F14.wireOp",EDGE,"E28.6.4.0"),sQuery(id+"F14.wireOp",EDGE,"E28.9.4.0"),sQuery(id+"F14.wireOp",EDGE,"E28.1.5.0"),sQuery(id+"F14.wireOp",EDGE,"E28.3.5.0"),sQuery(id+"F14.wireOp",EDGE,"E28.6.5.0"),sQuery(id+"F14.wireOp",EDGE,"E28.9.5.0"),sQuery(id+"F14.wireOp",EDGE,"E28.1.6.0"),sQuery(id+"F14.wireOp",EDGE,"E28.3.6.0"),sQuery(id+"F14.wireOp",EDGE,"E28.6.6.0"),sQuery(id+"F14.wireOp",EDGE,"E28.9.6.0"),sQuery(id+"F14.wireOp",EDGE,"E28.1.7.0"),sQuery(id+"F14.wireOp",EDGE,"E28.3.7.0"),sQuery(id+"F14.wireOp",EDGE,"E28.6.7.0"),sQuery(id+"F14.wireOp",EDGE,"E28.9.7.0"),sQuery(id+"F14.wireOp",EDGE,"E28.1.8.0"),sQuery(id+"F14.wireOp",EDGE,"E28.3.8.0"),sQuery(id+"F14.wireOp",EDGE,"E28.6.8.0"),sQuery(id+"F14.wireOp",EDGE,"E28.9.8.0"),sQuery(id+"F14.wireOp",EDGE,"E28.1.9.0"),sQuery(id+"F14.wireOp",EDGE,"E28.3.9.0"),sQuery(id+"F14.wireOp",EDGE,"E28.6.9.0"),sQuery(id+"F14.wireOp",EDGE,"E28.9.9.0"),sQuery(id+"F14.wireOp",EDGE,"E28.1.10.0"),sQuery(id+"F14.wireOp",EDGE,"E28.3.10.0"),sQuery(id+"F14.wireOp",EDGE,"E28.6.10.0"),sQuery(id+"F14.wireOp",EDGE,"E28.9.10.0"),sQuery(id+"F14.wireOp",EDGE,"E28.1.11.0"),sQuery(id+"F14.wireOp",EDGE,"E28.3.11.0"),sQuery(id+"F14.wireOp",EDGE,"E28.6.11.0"),sQuery(id+"F14.wireOp",EDGE,"E28.9.11.0"),sQuery(id+"F14.wireOp",EDGE,"E28.1.12.0"),sQuery(id+"F14.wireOp",EDGE,"E28.3.12.0"),sQuery(id+"F14.wireOp",EDGE,"E28.6.12.0"),sQuery(id+"F14.wireOp",EDGE,"E28.9.12.0"),sQuery(id+"F14.wireOp",EDGE,"E28.1.13.0"),sQuery(id+"F14.wireOp",EDGE,"E28.3.13.0"),sQuery(id+"F14.wireOp",EDGE,"E28.6.13.0"),sQuery(id+"F14.wireOp",EDGE,"E28.9.13.0"),sQuery(id+"F14.wireOp",EDGE,"E28.1.14.0"),sQuery(id+"F14.wireOp",EDGE,"E28.3.14.0"),sQuery(id+"F14.wireOp",EDGE,"E28.6.14.0"),sQuery(id+"F14.wireOp",EDGE,"E28.9.14.0"),sQuery(id+"F14.wireOp",EDGE,"E28.1.15.0"),sQuery(id+"F14.wireOp",EDGE,"E28.3.15.0"),sQuery(id+"F14.wireOp",EDGE,"E28.6.15.0"),sQuery(id+"F14.wireOp",EDGE,"E28.9.15.0"),sQuery(id+"F14.wireOp",EDGE,"E28.1.16.0"),sQuery(id+"F14.wireOp",EDGE,"E28.3.16.0"),sQuery(id+"F14.wireOp",EDGE,"E28.6.16.0"),sQuery(id+"F14.wireOp",EDGE,"E28.9.16.0"),sQuery(id+"F14.wireOp",EDGE,"E28.1.17.0"),sQuery(id+"F14.wireOp",EDGE,"E28.3.17.0"),sQuery(id+"F14.wireOp",EDGE,"E28.6.17.0"),sQuery(id+"F14.wireOp",EDGE,"E28.9.17.0"),sQuery(id+"F14.wireOp",EDGE,"E28.1.18.0"),sQuery(id+"F14.wireOp",EDGE,"E28.3.18.0"),sQuery(id+"F14.wireOp",EDGE,"E28.6.18.0"),sQuery(id+"F14.wireOp",EDGE,"E28.9.18.0"),sQuery(id+"F14.wireOp",EDGE,"E28.1.19.0"),sQuery(id+"F14.wireOp",EDGE,"E28.3.19.0"),sQuery(id+"F14.wireOp",EDGE,"E28.6.19.0"),sQuery(id+"F14.wireOp",EDGE,"E28.9.19.0"),sQuery(id+"F14.wireOp",EDGE,"E28.1.20.0"),sQuery(id+"F14.wireOp",EDGE,"E28.3.20.0"),sQuery(id+"F14.wireOp",EDGE,"E28.6.20.0"),sQuery(id+"F14.wireOp",EDGE,"E28.9.20.0"),sQuery(id+"F14.wireOp",EDGE,"E28.1.21.0"),sQuery(id+"F14.wireOp",EDGE,"E28.3.21.0"),sQuery(id+"F14.wireOp",EDGE,"E28.6.21.0"),sQuery(id+"F14.wireOp",EDGE,"E28.9.21.0"),sQuery(id+"F14.wireOp",EDGE,"E28.1.22.0"),sQuery(id+"F14.wireOp",EDGE,"E28.3.22.0"),sQuery(id+"F14.wireOp",EDGE,"E28.6.22.0"),sQuery(id+"F14.wireOp",EDGE,"E28.9.22.0"),sQuery(id+"F14.wireOp",EDGE,"E28.1.23.0"),sQuery(id+"F14.wireOp",EDGE,"E28.3.23.0"),sQuery(id+"F14.wireOp",EDGE,"E28.6.23.0"),sQuery(id+"F14.wireOp",EDGE,"E28.9.23.0"),sQuery(id+"F14.wireOp",EDGE,"E28.1.24.0"),sQuery(id+"F14.wireOp",EDGE,"E28.3.24.0"),sQuery(id+"F14.wireOp",EDGE,"E28.6.24.0"),sQuery(id+"F14.wireOp",EDGE,"E28.9.24.0"),sQuery(id+"F14.wireOp",EDGE,"E28.1.25.0"),sQuery(id+"F14.wireOp",EDGE,"E28.3.25.0"),sQuery(id+"F14.wireOp",EDGE,"E28.6.25.0"),sQuery(id+"F14.wireOp",EDGE,"E28.9.25.0"),sQuery(id+"F14.wireOp",EDGE,"E28.1.26.0"),sQuery(id+"F14.wireOp",EDGE,"E28.3.26.0"),sQuery(id+"F14.wireOp",EDGE,"E28.6.26.0"),sQuery(id+"F14.wireOp",EDGE,"E28.9.26.0"),sQuery(id+"F14.wireOp",EDGE,"E28.1.27.0"),sQuery(id+"F14.wireOp",EDGE,"E28.3.27.0"),sQuery(id+"F14.wireOp",EDGE,"E28.6.27.0"),sQuery(id+"F14.wireOp",EDGE,"E28.9.27.0"),sQuery(id+"F14.wireOp",EDGE,"E28.1.28.0"),sQuery(id+"F14.wireOp",EDGE,"E28.3.28.0"),sQuery(id+"F14.wireOp",EDGE,"E28.6.28.0"),sQuery(id+"F14.wireOp",EDGE,"E28.9.28.0"),sQuery(id+"F14.wireOp",EDGE,"E28.1.29.0"),sQuery(id+"F14.wireOp",EDGE,"E28.3.29.0"),sQuery(id+"F14.wireOp",EDGE,"E28.6.29.0"),sQuery(id+"F14.wireOp",EDGE,"E28.9.29.0"),sQuery(id+"F14.wireOp",EDGE,"E28.1.30.0"),sQuery(id+"F14.wireOp",EDGE,"E28.3.30.0"),sQuery(id+"F14.wireOp",EDGE,"E28.6.30.0"),sQuery(id+"F14.wireOp",EDGE,"E28.9.30.0"),sQuery(id+"F14.wireOp",EDGE,"E28.1.31.0"),sQuery(id+"F14.wireOp",EDGE,"E28.3.31.0"),sQuery(id+"F14.wireOp",EDGE,"E28.6.31.0"),sQuery(id+"F14.wireOp",EDGE,"E28.9.31.0"),sQuery(id+"F14.wireOp",EDGE,"E28.1.32.0"),sQuery(id+"F14.wireOp",EDGE,"E28.3.32.0"),sQuery(id+"F14.wireOp",EDGE,"E28.6.32.0"),sQuery(id+"F14.wireOp",EDGE,"E28.9.32.0"),sQuery(id+"F14.wireOp",EDGE,"E28.1.33.0"),sQuery(id+"F14.wireOp",EDGE,"E28.3.33.0"),sQuery(id+"F14.wireOp",EDGE,"E28.6.33.0"),sQuery(id+"F14.wireOp",EDGE,"E28.9.33.0"),sQuery(id+"F14.wireOp",EDGE,"E28.1.34.0"),sQuery(id+"F14.wireOp",EDGE,"E28.3.34.0"),sQuery(id+"F14.wireOp",EDGE,"E28.6.34.0"),sQuery(id+"F14.wireOp",EDGE,"E28.9.34.0"),sQuery(id+"F14.wireOp",EDGE,"E28.1.35.0"),sQuery(id+"F14.wireOp",EDGE,"E28.3.35.0"),sQuery(id+"F14.wireOp",EDGE,"E28.6.35.0"),sQuery(id+"F14.wireOp",EDGE,"E28.9.35.0"),sQuery(id+"F14.wireOp",EDGE,"E28.1.36.0"),sQuery(id+"F14.wireOp",EDGE,"E28.3.36.0"),sQuery(id+"F14.wireOp",EDGE,"E28.6.36.0"),sQuery(id+"F14.wireOp",EDGE,"E28.9.36.0"),sQuery(id+"F14.wireOp",EDGE,"E28.1.37.0"),sQuery(id+"F14.wireOp",EDGE,"E28.3.37.0"),sQuery(id+"F14.wireOp",EDGE,"E28.6.37.0"),sQuery(id+"F14.wireOp",EDGE,"E28.9.37.0"),sQuery(id+"F14.wireOp",EDGE,"E28.1.38.0"),sQuery(id+"F14.wireOp",EDGE,"E28.3.38.0"),sQuery(id+"F14.wireOp",EDGE,"E28.6.38.0"),sQuery(id+"F14.wireOp",EDGE,"E28.9.38.0"),sQuery(id+"F14.wireOp",EDGE,"E28.1.39.0"),sQuery(id+"F14.wireOp",EDGE,"E28.3.39.0"),sQuery(id+"F14.wireOp",EDGE,"E28.6.39.0"),sQuery(id+"F14.wireOp",EDGE,"E28.9.39.0")])],"isStart":false});
            var sketch = newSketch(context, id + "F31", { "sketchPlane" : qUnion([Q0])});
            skCircle(sketch, "E47.0", {"center": v(0, 0) * mm, "radius": 3 * mm});
            skCircle(sketch, "E48.0", {"center": v(0, 0) * mm, "radius": 5 * mm});
            skSolve(sketch);
        }
        {
            var Q0;
            Q0 = qSketchRegion(id + "F31", true);
            extrude(context, id + "F32", {"entities" : qUnion([Q0]), "operationType" : NewBodyOperationType.ADD, "depth" : 5 * mm, "offsetDistance" : 25 * mm});
        }
        {
            var Q0;
            Q0=makeQuery(id+"F32.opExtrude","CAP_FACE",FACE,{"disambiguationData":[OSD([sQuery(id+"F31.wireOp",EDGE,"E47.0"),sQuery(id+"F31.wireOp",EDGE,"E48.0")])],"isStart":false});
            var sketch = newSketch(context, id + "F33", { "sketchPlane" : qUnion([Q0])});
            skCircle(sketch, "E49.0", {"center": v(0, 0) * mm, "radius": 3 * mm});
            skCircle(sketch, "E50.0", {"center": v(0, 0) * mm, "radius": 5 * mm});
            skLineSegment(sketch, "E51", {"start": v(0, 50) * mm, "end": v(1.5, 50) * mm});
            skLineSegment(sketch, "E52", {"start": v(1.5, 50) * mm, "end": v(3, 4) * mm});
            skLineSegment(sketch, "E53.MirrorCS", {"start": v(0, 50) * mm, "end": v(-1.5, 50) * mm});
            skLineSegment(sketch, "E54.MirrorCS", {"start": v(-1.5, 50) * mm, "end": v(-3, 4) * mm});
            skSolve(sketch);
        }
        {
            var Q0;
            Q0 = qSketchRegion(id + "F33", true);
            extrude(context, id + "F34", {"entities" : qUnion([Q0]), "operationType" : NewBodyOperationType.ADD, "depth" : 1 * mm, "offsetDistance" : 25 * mm});
        }
        {
            var Q0;
            Q0=makeQuery(id+"F6.opExtrude","CAP_FACE",FACE,{"disambiguationData":[OSD([sQuery(id+"F0.wireOp",EDGE,"E0")])],"isStart":false});
            var sketch = newSketch(context, id + "F35", { "sketchPlane" : qUnion([Q0])});
            skCircle(sketch, "E55", {"center": v(0, 0) * mm, "radius": 5 * mm});
            skLineSegment(sketch, "E56", {"start": v(0, 80) * mm, "end": v(0.5, 80) * mm});
            skLineSegment(sketch, "E57", {"start": v(0.5, 80) * mm, "end": v(2, 4.58) * mm});
            skLineSegment(sketch, "E58.MirrorCS", {"start": v(0, 80) * mm, "end": v(-0.5, 80) * mm});
            skLineSegment(sketch, "E59.MirrorCS", {"start": v(-0.5, 80) * mm, "end": v(-2, 4.58) * mm});
            skSolve(sketch);
        }
        {
            var Q0;
            Q0 = qSketchRegion(id + "F35", true);
            extrude(context, id + "F36", {"entities" : qUnion([Q0]), "operationType" : NewBodyOperationType.ADD, "oppositeDirection" : true, "depth" : 1 * mm, "offsetDistance" : 25 * mm});
        }
    });
